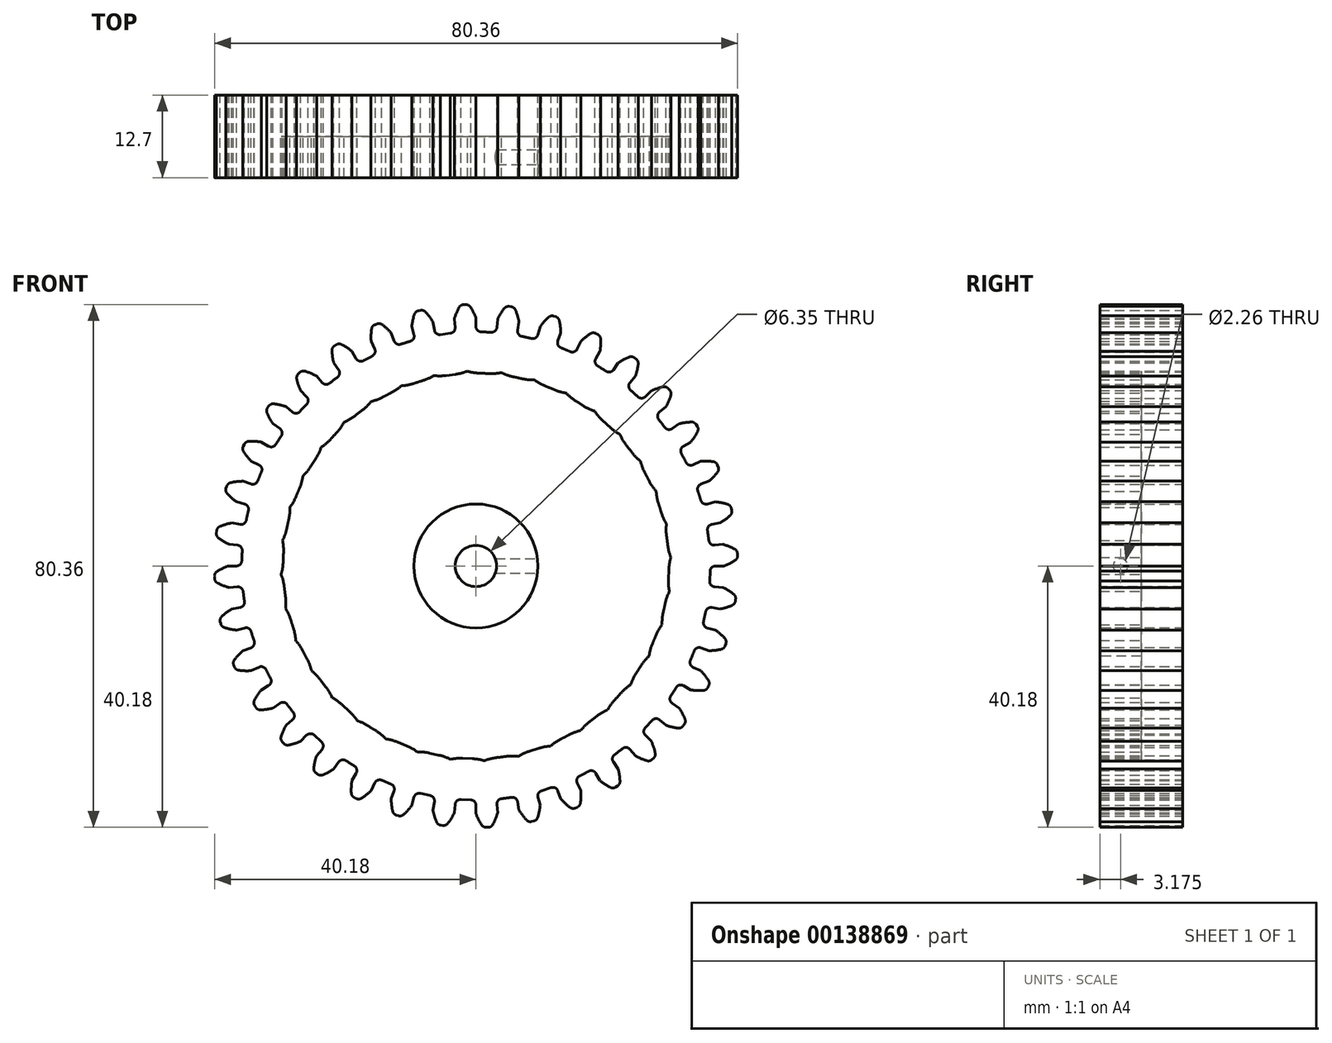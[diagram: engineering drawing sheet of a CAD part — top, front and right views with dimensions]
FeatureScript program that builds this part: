
annotation { "Feature Type Name" : "Feature", "Feature Type Description" : "" }
export const myFeature = defineFeature(function(context is Context, id is Id, definition is map)
    precondition{}
    {
        {
            var Q0;
            Q0=qCreatedBy(makeId("Front.planeOp"),FACE);
            var sketch = newSketch(context, id + "F0", { "sketchPlane" : qUnion([Q0])});
            skArc(sketch, "E0.trimOffspring", {"start": v(0, 38.1) * mm, "mid": v(-0.39, 38.97) * mm, "end": v(-0.86, 39.8) * mm});
            skLineSegment(sketch, "E1", {"start": v(0, 38.1) * mm, "end": v(0, 36.8) * mm});
            skLineSegment(sketch, "E2", {"start": v(-1.59, 40.18) * mm, "end": v(-1.75, 40.17) * mm});
            skLineSegment(sketch, "E3.MirrorCS", {"start": v(-1.92, 40.17) * mm, "end": v(-1.75, 40.17) * mm});
            skArc(sketch, "E4.MirrorCS", {"start": v(-3.32, 37.96) * mm, "mid": v(-3.01, 38.86) * mm, "end": v(-2.61, 39.72) * mm});
            skLineSegment(sketch, "E5.MirrorCS", {"start": v(-3.32, 37.96) * mm, "end": v(-3.2, 36.66) * mm});
            skPoint(sketch, "E6.visualSharp", {"position": v(-3.14, 35.85) * mm});
            skArc(sketch, "E6.filletArc", {"start": v(-3.94, 35.77) * mm, "mid": v(-3.4, 36.06) * mm, "end": v(-3.2, 36.66) * mm});
            skPoint(sketch, "E7.visualSharp", {"position": v(0, 35.98) * mm});
            skArc(sketch, "E7.filletArc", {"start": v(0, 36.8) * mm, "mid": v(0.24, 36.22) * mm, "end": v(0.8, 35.97) * mm});
            skArc(sketch, "E8.filletArc", {"start": v(-1.92, 40.17) * mm, "mid": v(-2.33, 40.04) * mm, "end": v(-2.61, 39.72) * mm});
            skArc(sketch, "E9.filletArc", {"start": v(-0.86, 39.8) * mm, "mid": v(-1.17, 40.09) * mm, "end": v(-1.59, 40.18) * mm});
            skArc(sketch, "E10.1.0", {"start": v(-10.1, 34.54) * mm, "mid": v(-9.6, 34.93) * mm, "end": v(-9.52, 35.55) * mm});
            skLineSegment(sketch, "E10.1.1", {"start": v(-9.86, 36.8) * mm, "end": v(-9.52, 35.55) * mm});
            skArc(sketch, "E10.1.2", {"start": v(-9.86, 36.8) * mm, "mid": v(-9.71, 37.74) * mm, "end": v(-9.47, 38.66) * mm});
            skArc(sketch, "E10.1.3", {"start": v(-8.86, 39.22) * mm, "mid": v(-9.24, 39.03) * mm, "end": v(-9.47, 38.66) * mm});
            skLineSegment(sketch, "E10.1.4", {"start": v(-8.86, 39.22) * mm, "end": v(-8.7, 39.26) * mm});
            skLineSegment(sketch, "E10.1.5", {"start": v(-8.54, 39.3) * mm, "end": v(-8.7, 39.26) * mm});
            skArc(sketch, "E10.1.6", {"start": v(-7.76, 39.05) * mm, "mid": v(-8.12, 39.28) * mm, "end": v(-8.54, 39.3) * mm});
            skArc(sketch, "E10.1.7", {"start": v(-6.62, 37.52) * mm, "mid": v(-7.15, 38.31) * mm, "end": v(-7.76, 39.05) * mm});
            skLineSegment(sketch, "E10.1.8", {"start": v(-6.62, 37.52) * mm, "end": v(-6.4, 36.24) * mm});
            skArc(sketch, "E10.1.9", {"start": v(-6.4, 36.24) * mm, "mid": v(-6.06, 35.71) * mm, "end": v(-5.45, 35.57) * mm});
            skArc(sketch, "E10.2.0", {"start": v(-15.93, 32.26) * mm, "mid": v(-15.52, 32.73) * mm, "end": v(-15.55, 33.35) * mm});
            skLineSegment(sketch, "E10.2.1", {"start": v(-16.1, 34.53) * mm, "end": v(-15.55, 33.35) * mm});
            skArc(sketch, "E10.2.2", {"start": v(-16.1, 34.53) * mm, "mid": v(-16.12, 35.48) * mm, "end": v(-16.04, 36.43) * mm});
            skArc(sketch, "E10.2.3", {"start": v(-15.54, 37.09) * mm, "mid": v(-15.88, 36.83) * mm, "end": v(-16.04, 36.43) * mm});
            skLineSegment(sketch, "E10.2.4", {"start": v(-15.54, 37.09) * mm, "end": v(-15.39, 37.15) * mm});
            skLineSegment(sketch, "E10.2.5", {"start": v(-15.24, 37.21) * mm, "end": v(-15.39, 37.15) * mm});
            skArc(sketch, "E10.2.6", {"start": v(-14.42, 37.1) * mm, "mid": v(-14.81, 37.27) * mm, "end": v(-15.24, 37.21) * mm});
            skArc(sketch, "E10.2.7", {"start": v(-13.03, 35.8) * mm, "mid": v(-13.7, 36.49) * mm, "end": v(-14.42, 37.1) * mm});
            skLineSegment(sketch, "E10.2.8", {"start": v(-13.03, 35.8) * mm, "end": v(-12.59, 34.58) * mm});
            skArc(sketch, "E10.2.9", {"start": v(-12.59, 34.58) * mm, "mid": v(-12.17, 34.12) * mm, "end": v(-11.55, 34.08) * mm});
            skArc(sketch, "E10.3.0", {"start": v(-21.3, 29) * mm, "mid": v(-20.97, 29.54) * mm, "end": v(-21.1, 30.14) * mm});
            skLineSegment(sketch, "E10.3.1", {"start": v(-21.85, 31.2) * mm, "end": v(-21.1, 30.14) * mm});
            skArc(sketch, "E10.3.2", {"start": v(-21.85, 31.2) * mm, "mid": v(-22.04, 32.14) * mm, "end": v(-22.13, 33.1) * mm});
            skArc(sketch, "E10.3.3", {"start": v(-21.74, 33.83) * mm, "mid": v(-22.03, 33.51) * mm, "end": v(-22.13, 33.1) * mm});
            skLineSegment(sketch, "E10.3.4", {"start": v(-21.74, 33.83) * mm, "end": v(-21.6, 33.91) * mm});
            skLineSegment(sketch, "E10.3.5", {"start": v(-21.47, 34) * mm, "end": v(-21.6, 33.91) * mm});
            skArc(sketch, "E10.3.6", {"start": v(-20.64, 34.04) * mm, "mid": v(-21.06, 34.13) * mm, "end": v(-21.47, 34) * mm});
            skArc(sketch, "E10.3.7", {"start": v(-19.05, 33) * mm, "mid": v(-19.82, 33.56) * mm, "end": v(-20.64, 34.04) * mm});
            skLineSegment(sketch, "E10.3.8", {"start": v(-19.05, 33) * mm, "end": v(-18.4, 31.87) * mm});
            skArc(sketch, "E10.3.9", {"start": v(-18.4, 31.87) * mm, "mid": v(-17.9, 31.49) * mm, "end": v(-17.29, 31.56) * mm});
            skArc(sketch, "E10.4.0", {"start": v(-26, 24.87) * mm, "mid": v(-25.78, 25.45) * mm, "end": v(-26.02, 26.02) * mm});
            skLineSegment(sketch, "E10.4.1", {"start": v(-26.94, 26.94) * mm, "end": v(-26.02, 26.02) * mm});
            skArc(sketch, "E10.4.2", {"start": v(-26.94, 26.94) * mm, "mid": v(-27.28, 27.83) * mm, "end": v(-27.54, 28.75) * mm});
            skArc(sketch, "E10.4.3", {"start": v(-27.29, 29.54) * mm, "mid": v(-27.52, 29.18) * mm, "end": v(-27.54, 28.75) * mm});
            skLineSegment(sketch, "E10.4.4", {"start": v(-27.29, 29.54) * mm, "end": v(-27.17, 29.65) * mm});
            skLineSegment(sketch, "E10.4.5", {"start": v(-27.05, 29.76) * mm, "end": v(-27.17, 29.65) * mm});
            skArc(sketch, "E10.4.6", {"start": v(-26.24, 29.94) * mm, "mid": v(-26.67, 29.96) * mm, "end": v(-27.05, 29.76) * mm});
            skArc(sketch, "E10.4.7", {"start": v(-24.5, 29.19) * mm, "mid": v(-25.35, 29.6) * mm, "end": v(-26.24, 29.94) * mm});
            skLineSegment(sketch, "E10.4.8", {"start": v(-24.5, 29.19) * mm, "end": v(-23.65, 28.2) * mm});
            skArc(sketch, "E10.4.9", {"start": v(-23.65, 28.2) * mm, "mid": v(-23.1, 27.9) * mm, "end": v(-22.5, 28.08) * mm});
            skArc(sketch, "E10.5.0", {"start": v(-29.93, 19.97) * mm, "mid": v(-29.8, 20.58) * mm, "end": v(-30.14, 21.1) * mm});
            skLineSegment(sketch, "E10.5.1", {"start": v(-31.2, 21.85) * mm, "end": v(-30.14, 21.1) * mm});
            skArc(sketch, "E10.5.2", {"start": v(-31.2, 21.85) * mm, "mid": v(-31.7, 22.67) * mm, "end": v(-32.1, 23.53) * mm});
            skArc(sketch, "E10.5.3", {"start": v(-32, 24.35) * mm, "mid": v(-32.17, 23.95) * mm, "end": v(-32.1, 23.53) * mm});
            skLineSegment(sketch, "E10.5.4", {"start": v(-32, 24.35) * mm, "end": v(-31.9, 24.48) * mm});
            skLineSegment(sketch, "E10.5.5", {"start": v(-31.8, 24.6) * mm, "end": v(-31.9, 24.48) * mm});
            skArc(sketch, "E10.5.6", {"start": v(-31.04, 24.93) * mm, "mid": v(-31.46, 24.87) * mm, "end": v(-31.8, 24.6) * mm});
            skArc(sketch, "E10.5.7", {"start": v(-29.19, 24.5) * mm, "mid": v(-30.1, 24.75) * mm, "end": v(-31.04, 24.93) * mm});
            skLineSegment(sketch, "E10.5.8", {"start": v(-29.19, 24.5) * mm, "end": v(-28.2, 23.65) * mm});
            skArc(sketch, "E10.5.9", {"start": v(-28.2, 23.65) * mm, "mid": v(-27.6, 23.46) * mm, "end": v(-27.04, 23.74) * mm});
            skArc(sketch, "E10.6.0", {"start": v(-32.94, 14.47) * mm, "mid": v(-32.93, 15.1) * mm, "end": v(-33.35, 15.55) * mm});
            skLineSegment(sketch, "E10.6.1", {"start": v(-34.53, 16.1) * mm, "end": v(-33.35, 15.55) * mm});
            skArc(sketch, "E10.6.2", {"start": v(-34.53, 16.1) * mm, "mid": v(-35.16, 16.82) * mm, "end": v(-35.7, 17.6) * mm});
            skArc(sketch, "E10.6.3", {"start": v(-35.74, 18.42) * mm, "mid": v(-35.84, 18) * mm, "end": v(-35.7, 17.6) * mm});
            skLineSegment(sketch, "E10.6.4", {"start": v(-35.74, 18.42) * mm, "end": v(-35.67, 18.57) * mm});
            skLineSegment(sketch, "E10.6.5", {"start": v(-35.6, 18.71) * mm, "end": v(-35.67, 18.57) * mm});
            skArc(sketch, "E10.6.6", {"start": v(-34.9, 19.16) * mm, "mid": v(-35.3, 19.03) * mm, "end": v(-35.6, 18.71) * mm});
            skArc(sketch, "E10.6.7", {"start": v(-33, 19.05) * mm, "mid": v(-33.94, 19.15) * mm, "end": v(-34.9, 19.16) * mm});
            skLineSegment(sketch, "E10.6.8", {"start": v(-33, 19.05) * mm, "end": v(-31.87, 18.4) * mm});
            skArc(sketch, "E10.6.9", {"start": v(-31.87, 18.4) * mm, "mid": v(-31.25, 18.31) * mm, "end": v(-30.75, 18.69) * mm});
            skArc(sketch, "E10.7.0", {"start": v(-34.96, 8.53) * mm, "mid": v(-35.05, 9.15) * mm, "end": v(-35.55, 9.52) * mm});
            skLineSegment(sketch, "E10.7.1", {"start": v(-36.8, 9.86) * mm, "end": v(-35.55, 9.52) * mm});
            skArc(sketch, "E10.7.2", {"start": v(-36.8, 9.86) * mm, "mid": v(-37.54, 10.46) * mm, "end": v(-38.22, 11.13) * mm});
            skArc(sketch, "E10.7.3", {"start": v(-38.4, 11.93) * mm, "mid": v(-38.42, 11.5) * mm, "end": v(-38.22, 11.13) * mm});
            skLineSegment(sketch, "E10.7.4", {"start": v(-38.4, 11.93) * mm, "end": v(-38.35, 12.1) * mm});
            skLineSegment(sketch, "E10.7.5", {"start": v(-38.3, 12.25) * mm, "end": v(-38.35, 12.1) * mm});
            skArc(sketch, "E10.7.6", {"start": v(-37.7, 12.8) * mm, "mid": v(-38.07, 12.6) * mm, "end": v(-38.3, 12.25) * mm});
            skArc(sketch, "E10.7.7", {"start": v(-35.8, 13.03) * mm, "mid": v(-36.75, 12.97) * mm, "end": v(-37.7, 12.8) * mm});
            skLineSegment(sketch, "E10.7.8", {"start": v(-35.8, 13.03) * mm, "end": v(-34.58, 12.59) * mm});
            skArc(sketch, "E10.7.9", {"start": v(-34.58, 12.59) * mm, "mid": v(-33.96, 12.6) * mm, "end": v(-33.53, 13.06) * mm});
            skArc(sketch, "E10.8.0", {"start": v(-35.9, 2.33) * mm, "mid": v(-36.1, 2.92) * mm, "end": v(-36.66, 3.2) * mm});
            skLineSegment(sketch, "E10.8.1", {"start": v(-37.96, 3.32) * mm, "end": v(-36.66, 3.2) * mm});
            skArc(sketch, "E10.8.2", {"start": v(-37.96, 3.32) * mm, "mid": v(-38.79, 3.78) * mm, "end": v(-39.57, 4.32) * mm});
            skArc(sketch, "E10.8.3", {"start": v(-39.89, 5.09) * mm, "mid": v(-39.83, 4.66) * mm, "end": v(-39.57, 4.32) * mm});
            skLineSegment(sketch, "E10.8.4", {"start": v(-39.89, 5.09) * mm, "end": v(-39.87, 5.25) * mm});
            skLineSegment(sketch, "E10.8.5", {"start": v(-39.85, 5.41) * mm, "end": v(-39.87, 5.25) * mm});
            skArc(sketch, "E10.8.6", {"start": v(-39.34, 6.07) * mm, "mid": v(-39.68, 5.8) * mm, "end": v(-39.85, 5.41) * mm});
            skArc(sketch, "E10.8.7", {"start": v(-37.52, 6.62) * mm, "mid": v(-38.45, 6.39) * mm, "end": v(-39.34, 6.07) * mm});
            skLineSegment(sketch, "E10.8.8", {"start": v(-37.52, 6.62) * mm, "end": v(-36.24, 6.4) * mm});
            skArc(sketch, "E10.8.9", {"start": v(-36.24, 6.4) * mm, "mid": v(-35.63, 6.52) * mm, "end": v(-35.29, 7.04) * mm});
            skArc(sketch, "E10.9.0", {"start": v(-35.77, -3.94) * mm, "mid": v(-36.06, -3.4) * mm, "end": v(-36.66, -3.2) * mm});
            skLineSegment(sketch, "E10.9.1", {"start": v(-37.96, -3.32) * mm, "end": v(-36.66, -3.2) * mm});
            skArc(sketch, "E10.9.2", {"start": v(-37.96, -3.32) * mm, "mid": v(-38.86, -3.01) * mm, "end": v(-39.72, -2.61) * mm});
            skArc(sketch, "E10.9.3", {"start": v(-40.17, -1.92) * mm, "mid": v(-40.04, -2.33) * mm, "end": v(-39.72, -2.61) * mm});
            skLineSegment(sketch, "E10.9.4", {"start": v(-40.17, -1.92) * mm, "end": v(-40.17, -1.75) * mm});
            skLineSegment(sketch, "E10.9.5", {"start": v(-40.18, -1.59) * mm, "end": v(-40.17, -1.75) * mm});
            skArc(sketch, "E10.9.6", {"start": v(-39.8, -0.86) * mm, "mid": v(-40.09, -1.17) * mm, "end": v(-40.18, -1.59) * mm});
            skArc(sketch, "E10.9.7", {"start": v(-38.1, 0) * mm, "mid": v(-38.97, -0.39) * mm, "end": v(-39.8, -0.86) * mm});
            skLineSegment(sketch, "E10.9.8", {"start": v(-38.1, 0) * mm, "end": v(-36.8, 0) * mm});
            skArc(sketch, "E10.9.9", {"start": v(-36.8, 0) * mm, "mid": v(-36.22, 0.24) * mm, "end": v(-35.97, 0.8) * mm});
            skArc(sketch, "E10.10.0", {"start": v(-34.54, -10.1) * mm, "mid": v(-34.93, -9.6) * mm, "end": v(-35.55, -9.52) * mm});
            skLineSegment(sketch, "E10.10.1", {"start": v(-36.8, -9.86) * mm, "end": v(-35.55, -9.52) * mm});
            skArc(sketch, "E10.10.2", {"start": v(-36.8, -9.86) * mm, "mid": v(-37.74, -9.71) * mm, "end": v(-38.66, -9.47) * mm});
            skArc(sketch, "E10.10.3", {"start": v(-39.22, -8.86) * mm, "mid": v(-39.03, -9.24) * mm, "end": v(-38.66, -9.47) * mm});
            skLineSegment(sketch, "E10.10.4", {"start": v(-39.22, -8.86) * mm, "end": v(-39.26, -8.7) * mm});
            skLineSegment(sketch, "E10.10.5", {"start": v(-39.3, -8.54) * mm, "end": v(-39.26, -8.7) * mm});
            skArc(sketch, "E10.10.6", {"start": v(-39.05, -7.76) * mm, "mid": v(-39.28, -8.12) * mm, "end": v(-39.3, -8.54) * mm});
            skArc(sketch, "E10.10.7", {"start": v(-37.52, -6.62) * mm, "mid": v(-38.31, -7.15) * mm, "end": v(-39.05, -7.76) * mm});
            skLineSegment(sketch, "E10.10.8", {"start": v(-37.52, -6.62) * mm, "end": v(-36.24, -6.4) * mm});
            skArc(sketch, "E10.10.9", {"start": v(-36.24, -6.4) * mm, "mid": v(-35.71, -6.06) * mm, "end": v(-35.57, -5.45) * mm});
            skArc(sketch, "E10.11.0", {"start": v(-32.26, -15.93) * mm, "mid": v(-32.73, -15.52) * mm, "end": v(-33.35, -15.55) * mm});
            skLineSegment(sketch, "E10.11.1", {"start": v(-34.53, -16.1) * mm, "end": v(-33.35, -15.55) * mm});
            skArc(sketch, "E10.11.2", {"start": v(-34.53, -16.1) * mm, "mid": v(-35.48, -16.12) * mm, "end": v(-36.43, -16.04) * mm});
            skArc(sketch, "E10.11.3", {"start": v(-37.09, -15.54) * mm, "mid": v(-36.83, -15.88) * mm, "end": v(-36.43, -16.04) * mm});
            skLineSegment(sketch, "E10.11.4", {"start": v(-37.09, -15.54) * mm, "end": v(-37.15, -15.39) * mm});
            skLineSegment(sketch, "E10.11.5", {"start": v(-37.21, -15.24) * mm, "end": v(-37.15, -15.39) * mm});
            skArc(sketch, "E10.11.6", {"start": v(-37.1, -14.42) * mm, "mid": v(-37.27, -14.81) * mm, "end": v(-37.21, -15.24) * mm});
            skArc(sketch, "E10.11.7", {"start": v(-35.8, -13.03) * mm, "mid": v(-36.49, -13.7) * mm, "end": v(-37.1, -14.42) * mm});
            skLineSegment(sketch, "E10.11.8", {"start": v(-35.8, -13.03) * mm, "end": v(-34.58, -12.59) * mm});
            skArc(sketch, "E10.11.9", {"start": v(-34.58, -12.59) * mm, "mid": v(-34.12, -12.17) * mm, "end": v(-34.08, -11.55) * mm});
            skArc(sketch, "E10.12.0", {"start": v(-29, -21.3) * mm, "mid": v(-29.54, -20.97) * mm, "end": v(-30.14, -21.1) * mm});
            skLineSegment(sketch, "E10.12.1", {"start": v(-31.2, -21.85) * mm, "end": v(-30.14, -21.1) * mm});
            skArc(sketch, "E10.12.2", {"start": v(-31.2, -21.85) * mm, "mid": v(-32.14, -22.04) * mm, "end": v(-33.1, -22.13) * mm});
            skArc(sketch, "E10.12.3", {"start": v(-33.83, -21.74) * mm, "mid": v(-33.51, -22.03) * mm, "end": v(-33.1, -22.13) * mm});
            skLineSegment(sketch, "E10.12.4", {"start": v(-33.83, -21.74) * mm, "end": v(-33.91, -21.6) * mm});
            skLineSegment(sketch, "E10.12.5", {"start": v(-34, -21.47) * mm, "end": v(-33.91, -21.6) * mm});
            skArc(sketch, "E10.12.6", {"start": v(-34.04, -20.64) * mm, "mid": v(-34.13, -21.06) * mm, "end": v(-34, -21.47) * mm});
            skArc(sketch, "E10.12.7", {"start": v(-33, -19.05) * mm, "mid": v(-33.56, -19.82) * mm, "end": v(-34.04, -20.64) * mm});
            skLineSegment(sketch, "E10.12.8", {"start": v(-33, -19.05) * mm, "end": v(-31.87, -18.4) * mm});
            skArc(sketch, "E10.12.9", {"start": v(-31.87, -18.4) * mm, "mid": v(-31.49, -17.9) * mm, "end": v(-31.56, -17.29) * mm});
            skArc(sketch, "E10.13.0", {"start": v(-24.87, -26) * mm, "mid": v(-25.45, -25.78) * mm, "end": v(-26.02, -26.02) * mm});
            skLineSegment(sketch, "E10.13.1", {"start": v(-26.94, -26.94) * mm, "end": v(-26.02, -26.02) * mm});
            skArc(sketch, "E10.13.2", {"start": v(-26.94, -26.94) * mm, "mid": v(-27.83, -27.28) * mm, "end": v(-28.75, -27.54) * mm});
            skArc(sketch, "E10.13.3", {"start": v(-29.54, -27.29) * mm, "mid": v(-29.18, -27.52) * mm, "end": v(-28.75, -27.54) * mm});
            skLineSegment(sketch, "E10.13.4", {"start": v(-29.54, -27.29) * mm, "end": v(-29.65, -27.17) * mm});
            skLineSegment(sketch, "E10.13.5", {"start": v(-29.76, -27.05) * mm, "end": v(-29.65, -27.17) * mm});
            skArc(sketch, "E10.13.6", {"start": v(-29.94, -26.24) * mm, "mid": v(-29.96, -26.67) * mm, "end": v(-29.76, -27.05) * mm});
            skArc(sketch, "E10.13.7", {"start": v(-29.19, -24.5) * mm, "mid": v(-29.6, -25.35) * mm, "end": v(-29.94, -26.24) * mm});
            skLineSegment(sketch, "E10.13.8", {"start": v(-29.19, -24.5) * mm, "end": v(-28.2, -23.65) * mm});
            skArc(sketch, "E10.13.9", {"start": v(-28.2, -23.65) * mm, "mid": v(-27.9, -23.1) * mm, "end": v(-28.08, -22.5) * mm});
            skArc(sketch, "E10.14.0", {"start": v(-19.97, -29.93) * mm, "mid": v(-20.58, -29.8) * mm, "end": v(-21.1, -30.14) * mm});
            skLineSegment(sketch, "E10.14.1", {"start": v(-21.85, -31.2) * mm, "end": v(-21.1, -30.14) * mm});
            skArc(sketch, "E10.14.2", {"start": v(-21.85, -31.2) * mm, "mid": v(-22.67, -31.7) * mm, "end": v(-23.53, -32.1) * mm});
            skArc(sketch, "E10.14.3", {"start": v(-24.35, -32) * mm, "mid": v(-23.95, -32.17) * mm, "end": v(-23.53, -32.1) * mm});
            skLineSegment(sketch, "E10.14.4", {"start": v(-24.35, -32) * mm, "end": v(-24.48, -31.9) * mm});
            skLineSegment(sketch, "E10.14.5", {"start": v(-24.6, -31.8) * mm, "end": v(-24.48, -31.9) * mm});
            skArc(sketch, "E10.14.6", {"start": v(-24.93, -31.04) * mm, "mid": v(-24.87, -31.46) * mm, "end": v(-24.6, -31.8) * mm});
            skArc(sketch, "E10.14.7", {"start": v(-24.5, -29.19) * mm, "mid": v(-24.75, -30.1) * mm, "end": v(-24.93, -31.04) * mm});
            skLineSegment(sketch, "E10.14.8", {"start": v(-24.5, -29.19) * mm, "end": v(-23.65, -28.2) * mm});
            skArc(sketch, "E10.14.9", {"start": v(-23.65, -28.2) * mm, "mid": v(-23.46, -27.6) * mm, "end": v(-23.74, -27.04) * mm});
            skArc(sketch, "E10.15.0", {"start": v(-14.47, -32.94) * mm, "mid": v(-15.1, -32.93) * mm, "end": v(-15.55, -33.35) * mm});
            skLineSegment(sketch, "E10.15.1", {"start": v(-16.1, -34.53) * mm, "end": v(-15.55, -33.35) * mm});
            skArc(sketch, "E10.15.2", {"start": v(-16.1, -34.53) * mm, "mid": v(-16.82, -35.16) * mm, "end": v(-17.6, -35.7) * mm});
            skArc(sketch, "E10.15.3", {"start": v(-18.42, -35.74) * mm, "mid": v(-18, -35.84) * mm, "end": v(-17.6, -35.7) * mm});
            skLineSegment(sketch, "E10.15.4", {"start": v(-18.42, -35.74) * mm, "end": v(-18.57, -35.67) * mm});
            skLineSegment(sketch, "E10.15.5", {"start": v(-18.71, -35.6) * mm, "end": v(-18.57, -35.67) * mm});
            skArc(sketch, "E10.15.6", {"start": v(-19.16, -34.9) * mm, "mid": v(-19.03, -35.3) * mm, "end": v(-18.71, -35.6) * mm});
            skArc(sketch, "E10.15.7", {"start": v(-19.05, -33) * mm, "mid": v(-19.15, -33.94) * mm, "end": v(-19.16, -34.9) * mm});
            skLineSegment(sketch, "E10.15.8", {"start": v(-19.05, -33) * mm, "end": v(-18.4, -31.87) * mm});
            skArc(sketch, "E10.15.9", {"start": v(-18.4, -31.87) * mm, "mid": v(-18.31, -31.25) * mm, "end": v(-18.69, -30.75) * mm});
            skArc(sketch, "E10.16.0", {"start": v(-8.53, -34.96) * mm, "mid": v(-9.15, -35.05) * mm, "end": v(-9.52, -35.55) * mm});
            skLineSegment(sketch, "E10.16.1", {"start": v(-9.86, -36.8) * mm, "end": v(-9.52, -35.55) * mm});
            skArc(sketch, "E10.16.2", {"start": v(-9.86, -36.8) * mm, "mid": v(-10.46, -37.54) * mm, "end": v(-11.13, -38.22) * mm});
            skArc(sketch, "E10.16.3", {"start": v(-11.93, -38.4) * mm, "mid": v(-11.5, -38.42) * mm, "end": v(-11.13, -38.22) * mm});
            skLineSegment(sketch, "E10.16.4", {"start": v(-11.93, -38.4) * mm, "end": v(-12.1, -38.35) * mm});
            skLineSegment(sketch, "E10.16.5", {"start": v(-12.25, -38.3) * mm, "end": v(-12.1, -38.35) * mm});
            skArc(sketch, "E10.16.6", {"start": v(-12.8, -37.7) * mm, "mid": v(-12.6, -38.07) * mm, "end": v(-12.25, -38.3) * mm});
            skArc(sketch, "E10.16.7", {"start": v(-13.03, -35.8) * mm, "mid": v(-12.97, -36.75) * mm, "end": v(-12.8, -37.7) * mm});
            skLineSegment(sketch, "E10.16.8", {"start": v(-13.03, -35.8) * mm, "end": v(-12.59, -34.58) * mm});
            skArc(sketch, "E10.16.9", {"start": v(-12.59, -34.58) * mm, "mid": v(-12.6, -33.96) * mm, "end": v(-13.06, -33.53) * mm});
            skArc(sketch, "E10.17.0", {"start": v(-2.33, -35.9) * mm, "mid": v(-2.92, -36.1) * mm, "end": v(-3.2, -36.66) * mm});
            skLineSegment(sketch, "E10.17.1", {"start": v(-3.32, -37.96) * mm, "end": v(-3.2, -36.66) * mm});
            skArc(sketch, "E10.17.2", {"start": v(-3.32, -37.96) * mm, "mid": v(-3.78, -38.79) * mm, "end": v(-4.32, -39.57) * mm});
            skArc(sketch, "E10.17.3", {"start": v(-5.09, -39.89) * mm, "mid": v(-4.66, -39.83) * mm, "end": v(-4.32, -39.57) * mm});
            skLineSegment(sketch, "E10.17.4", {"start": v(-5.09, -39.89) * mm, "end": v(-5.25, -39.87) * mm});
            skLineSegment(sketch, "E10.17.5", {"start": v(-5.41, -39.85) * mm, "end": v(-5.25, -39.87) * mm});
            skArc(sketch, "E10.17.6", {"start": v(-6.07, -39.34) * mm, "mid": v(-5.8, -39.68) * mm, "end": v(-5.41, -39.85) * mm});
            skArc(sketch, "E10.17.7", {"start": v(-6.62, -37.52) * mm, "mid": v(-6.39, -38.45) * mm, "end": v(-6.07, -39.34) * mm});
            skLineSegment(sketch, "E10.17.8", {"start": v(-6.62, -37.52) * mm, "end": v(-6.4, -36.24) * mm});
            skArc(sketch, "E10.17.9", {"start": v(-6.4, -36.24) * mm, "mid": v(-6.52, -35.63) * mm, "end": v(-7.04, -35.29) * mm});
            skArc(sketch, "E10.18.0", {"start": v(3.94, -35.77) * mm, "mid": v(3.4, -36.06) * mm, "end": v(3.2, -36.66) * mm});
            skLineSegment(sketch, "E10.18.1", {"start": v(3.32, -37.96) * mm, "end": v(3.2, -36.66) * mm});
            skArc(sketch, "E10.18.2", {"start": v(3.32, -37.96) * mm, "mid": v(3.01, -38.86) * mm, "end": v(2.61, -39.72) * mm});
            skArc(sketch, "E10.18.3", {"start": v(1.92, -40.17) * mm, "mid": v(2.33, -40.04) * mm, "end": v(2.61, -39.72) * mm});
            skLineSegment(sketch, "E10.18.4", {"start": v(1.92, -40.17) * mm, "end": v(1.75, -40.17) * mm});
            skLineSegment(sketch, "E10.18.5", {"start": v(1.59, -40.18) * mm, "end": v(1.75, -40.17) * mm});
            skArc(sketch, "E10.18.6", {"start": v(0.86, -39.8) * mm, "mid": v(1.17, -40.09) * mm, "end": v(1.59, -40.18) * mm});
            skArc(sketch, "E10.18.7", {"start": v(0, -38.1) * mm, "mid": v(0.39, -38.97) * mm, "end": v(0.86, -39.8) * mm});
            skLineSegment(sketch, "E10.18.8", {"start": v(0, -38.1) * mm, "end": v(0, -36.8) * mm});
            skArc(sketch, "E10.18.9", {"start": v(0, -36.8) * mm, "mid": v(-0.24, -36.22) * mm, "end": v(-0.8, -35.97) * mm});
            skArc(sketch, "E10.19.0", {"start": v(10.1, -34.54) * mm, "mid": v(9.6, -34.93) * mm, "end": v(9.52, -35.55) * mm});
            skLineSegment(sketch, "E10.19.1", {"start": v(9.86, -36.8) * mm, "end": v(9.52, -35.55) * mm});
            skArc(sketch, "E10.19.2", {"start": v(9.86, -36.8) * mm, "mid": v(9.71, -37.74) * mm, "end": v(9.47, -38.66) * mm});
            skArc(sketch, "E10.19.3", {"start": v(8.86, -39.22) * mm, "mid": v(9.24, -39.03) * mm, "end": v(9.47, -38.66) * mm});
            skLineSegment(sketch, "E10.19.4", {"start": v(8.86, -39.22) * mm, "end": v(8.7, -39.26) * mm});
            skLineSegment(sketch, "E10.19.5", {"start": v(8.54, -39.3) * mm, "end": v(8.7, -39.26) * mm});
            skArc(sketch, "E10.19.6", {"start": v(7.76, -39.05) * mm, "mid": v(8.12, -39.28) * mm, "end": v(8.54, -39.3) * mm});
            skArc(sketch, "E10.19.7", {"start": v(6.62, -37.52) * mm, "mid": v(7.15, -38.31) * mm, "end": v(7.76, -39.05) * mm});
            skLineSegment(sketch, "E10.19.8", {"start": v(6.62, -37.52) * mm, "end": v(6.4, -36.24) * mm});
            skArc(sketch, "E10.19.9", {"start": v(6.4, -36.24) * mm, "mid": v(6.06, -35.71) * mm, "end": v(5.45, -35.57) * mm});
            skArc(sketch, "E10.20.0", {"start": v(15.93, -32.26) * mm, "mid": v(15.52, -32.73) * mm, "end": v(15.55, -33.35) * mm});
            skLineSegment(sketch, "E10.20.1", {"start": v(16.1, -34.53) * mm, "end": v(15.55, -33.35) * mm});
            skArc(sketch, "E10.20.2", {"start": v(16.1, -34.53) * mm, "mid": v(16.12, -35.48) * mm, "end": v(16.04, -36.43) * mm});
            skArc(sketch, "E10.20.3", {"start": v(15.54, -37.09) * mm, "mid": v(15.88, -36.83) * mm, "end": v(16.04, -36.43) * mm});
            skLineSegment(sketch, "E10.20.4", {"start": v(15.54, -37.09) * mm, "end": v(15.39, -37.15) * mm});
            skLineSegment(sketch, "E10.20.5", {"start": v(15.24, -37.21) * mm, "end": v(15.39, -37.15) * mm});
            skArc(sketch, "E10.20.6", {"start": v(14.42, -37.1) * mm, "mid": v(14.81, -37.27) * mm, "end": v(15.24, -37.21) * mm});
            skArc(sketch, "E10.20.7", {"start": v(13.03, -35.8) * mm, "mid": v(13.7, -36.49) * mm, "end": v(14.42, -37.1) * mm});
            skLineSegment(sketch, "E10.20.8", {"start": v(13.03, -35.8) * mm, "end": v(12.59, -34.58) * mm});
            skArc(sketch, "E10.20.9", {"start": v(12.59, -34.58) * mm, "mid": v(12.17, -34.12) * mm, "end": v(11.55, -34.08) * mm});
            skArc(sketch, "E10.21.0", {"start": v(21.3, -29) * mm, "mid": v(20.97, -29.54) * mm, "end": v(21.1, -30.14) * mm});
            skLineSegment(sketch, "E10.21.1", {"start": v(21.85, -31.2) * mm, "end": v(21.1, -30.14) * mm});
            skArc(sketch, "E10.21.2", {"start": v(21.85, -31.2) * mm, "mid": v(22.04, -32.14) * mm, "end": v(22.13, -33.1) * mm});
            skArc(sketch, "E10.21.3", {"start": v(21.74, -33.83) * mm, "mid": v(22.03, -33.51) * mm, "end": v(22.13, -33.1) * mm});
            skLineSegment(sketch, "E10.21.4", {"start": v(21.74, -33.83) * mm, "end": v(21.6, -33.91) * mm});
            skLineSegment(sketch, "E10.21.5", {"start": v(21.47, -34) * mm, "end": v(21.6, -33.91) * mm});
            skArc(sketch, "E10.21.6", {"start": v(20.64, -34.04) * mm, "mid": v(21.06, -34.13) * mm, "end": v(21.47, -34) * mm});
            skArc(sketch, "E10.21.7", {"start": v(19.05, -33) * mm, "mid": v(19.82, -33.56) * mm, "end": v(20.64, -34.04) * mm});
            skLineSegment(sketch, "E10.21.8", {"start": v(19.05, -33) * mm, "end": v(18.4, -31.87) * mm});
            skArc(sketch, "E10.21.9", {"start": v(18.4, -31.87) * mm, "mid": v(17.9, -31.49) * mm, "end": v(17.29, -31.56) * mm});
            skArc(sketch, "E10.22.0", {"start": v(26, -24.87) * mm, "mid": v(25.78, -25.45) * mm, "end": v(26.02, -26.02) * mm});
            skLineSegment(sketch, "E10.22.1", {"start": v(26.94, -26.94) * mm, "end": v(26.02, -26.02) * mm});
            skArc(sketch, "E10.22.2", {"start": v(26.94, -26.94) * mm, "mid": v(27.28, -27.83) * mm, "end": v(27.54, -28.75) * mm});
            skArc(sketch, "E10.22.3", {"start": v(27.29, -29.54) * mm, "mid": v(27.52, -29.18) * mm, "end": v(27.54, -28.75) * mm});
            skLineSegment(sketch, "E10.22.4", {"start": v(27.29, -29.54) * mm, "end": v(27.17, -29.65) * mm});
            skLineSegment(sketch, "E10.22.5", {"start": v(27.05, -29.76) * mm, "end": v(27.17, -29.65) * mm});
            skArc(sketch, "E10.22.6", {"start": v(26.24, -29.94) * mm, "mid": v(26.67, -29.96) * mm, "end": v(27.05, -29.76) * mm});
            skArc(sketch, "E10.22.7", {"start": v(24.5, -29.19) * mm, "mid": v(25.35, -29.6) * mm, "end": v(26.24, -29.94) * mm});
            skLineSegment(sketch, "E10.22.8", {"start": v(24.5, -29.19) * mm, "end": v(23.65, -28.2) * mm});
            skArc(sketch, "E10.22.9", {"start": v(23.65, -28.2) * mm, "mid": v(23.1, -27.9) * mm, "end": v(22.5, -28.08) * mm});
            skArc(sketch, "E10.23.0", {"start": v(29.93, -19.97) * mm, "mid": v(29.8, -20.58) * mm, "end": v(30.14, -21.1) * mm});
            skLineSegment(sketch, "E10.23.1", {"start": v(31.2, -21.85) * mm, "end": v(30.14, -21.1) * mm});
            skArc(sketch, "E10.23.2", {"start": v(31.2, -21.85) * mm, "mid": v(31.7, -22.67) * mm, "end": v(32.1, -23.53) * mm});
            skArc(sketch, "E10.23.3", {"start": v(32, -24.35) * mm, "mid": v(32.17, -23.95) * mm, "end": v(32.1, -23.53) * mm});
            skLineSegment(sketch, "E10.23.4", {"start": v(32, -24.35) * mm, "end": v(31.9, -24.48) * mm});
            skLineSegment(sketch, "E10.23.5", {"start": v(31.8, -24.6) * mm, "end": v(31.9, -24.48) * mm});
            skArc(sketch, "E10.23.6", {"start": v(31.04, -24.93) * mm, "mid": v(31.46, -24.87) * mm, "end": v(31.8, -24.6) * mm});
            skArc(sketch, "E10.23.7", {"start": v(29.19, -24.5) * mm, "mid": v(30.1, -24.75) * mm, "end": v(31.04, -24.93) * mm});
            skLineSegment(sketch, "E10.23.8", {"start": v(29.19, -24.5) * mm, "end": v(28.2, -23.65) * mm});
            skArc(sketch, "E10.23.9", {"start": v(28.2, -23.65) * mm, "mid": v(27.6, -23.46) * mm, "end": v(27.04, -23.74) * mm});
            skArc(sketch, "E10.24.0", {"start": v(32.94, -14.47) * mm, "mid": v(32.93, -15.1) * mm, "end": v(33.35, -15.55) * mm});
            skLineSegment(sketch, "E10.24.1", {"start": v(34.53, -16.1) * mm, "end": v(33.35, -15.55) * mm});
            skArc(sketch, "E10.24.2", {"start": v(34.53, -16.1) * mm, "mid": v(35.16, -16.82) * mm, "end": v(35.7, -17.6) * mm});
            skArc(sketch, "E10.24.3", {"start": v(35.74, -18.42) * mm, "mid": v(35.84, -18) * mm, "end": v(35.7, -17.6) * mm});
            skLineSegment(sketch, "E10.24.4", {"start": v(35.74, -18.42) * mm, "end": v(35.67, -18.57) * mm});
            skLineSegment(sketch, "E10.24.5", {"start": v(35.6, -18.71) * mm, "end": v(35.67, -18.57) * mm});
            skArc(sketch, "E10.24.6", {"start": v(34.9, -19.16) * mm, "mid": v(35.3, -19.03) * mm, "end": v(35.6, -18.71) * mm});
            skArc(sketch, "E10.24.7", {"start": v(33, -19.05) * mm, "mid": v(33.94, -19.15) * mm, "end": v(34.9, -19.16) * mm});
            skLineSegment(sketch, "E10.24.8", {"start": v(33, -19.05) * mm, "end": v(31.87, -18.4) * mm});
            skArc(sketch, "E10.24.9", {"start": v(31.87, -18.4) * mm, "mid": v(31.25, -18.31) * mm, "end": v(30.75, -18.69) * mm});
            skArc(sketch, "E10.25.0", {"start": v(34.96, -8.53) * mm, "mid": v(35.05, -9.15) * mm, "end": v(35.55, -9.52) * mm});
            skLineSegment(sketch, "E10.25.1", {"start": v(36.8, -9.86) * mm, "end": v(35.55, -9.52) * mm});
            skArc(sketch, "E10.25.2", {"start": v(36.8, -9.86) * mm, "mid": v(37.54, -10.46) * mm, "end": v(38.22, -11.13) * mm});
            skArc(sketch, "E10.25.3", {"start": v(38.4, -11.93) * mm, "mid": v(38.42, -11.5) * mm, "end": v(38.22, -11.13) * mm});
            skLineSegment(sketch, "E10.25.4", {"start": v(38.4, -11.93) * mm, "end": v(38.35, -12.1) * mm});
            skLineSegment(sketch, "E10.25.5", {"start": v(38.3, -12.25) * mm, "end": v(38.35, -12.1) * mm});
            skArc(sketch, "E10.25.6", {"start": v(37.7, -12.8) * mm, "mid": v(38.07, -12.6) * mm, "end": v(38.3, -12.25) * mm});
            skArc(sketch, "E10.25.7", {"start": v(35.8, -13.03) * mm, "mid": v(36.75, -12.97) * mm, "end": v(37.7, -12.8) * mm});
            skLineSegment(sketch, "E10.25.8", {"start": v(35.8, -13.03) * mm, "end": v(34.58, -12.59) * mm});
            skArc(sketch, "E10.25.9", {"start": v(34.58, -12.59) * mm, "mid": v(33.96, -12.6) * mm, "end": v(33.53, -13.06) * mm});
            skArc(sketch, "E10.26.0", {"start": v(35.9, -2.33) * mm, "mid": v(36.1, -2.92) * mm, "end": v(36.66, -3.2) * mm});
            skLineSegment(sketch, "E10.26.1", {"start": v(37.96, -3.32) * mm, "end": v(36.66, -3.2) * mm});
            skArc(sketch, "E10.26.2", {"start": v(37.96, -3.32) * mm, "mid": v(38.79, -3.78) * mm, "end": v(39.57, -4.32) * mm});
            skArc(sketch, "E10.26.3", {"start": v(39.89, -5.09) * mm, "mid": v(39.83, -4.66) * mm, "end": v(39.57, -4.32) * mm});
            skLineSegment(sketch, "E10.26.4", {"start": v(39.89, -5.09) * mm, "end": v(39.87, -5.25) * mm});
            skLineSegment(sketch, "E10.26.5", {"start": v(39.85, -5.41) * mm, "end": v(39.87, -5.25) * mm});
            skArc(sketch, "E10.26.6", {"start": v(39.34, -6.07) * mm, "mid": v(39.68, -5.8) * mm, "end": v(39.85, -5.41) * mm});
            skArc(sketch, "E10.26.7", {"start": v(37.52, -6.62) * mm, "mid": v(38.45, -6.39) * mm, "end": v(39.34, -6.07) * mm});
            skLineSegment(sketch, "E10.26.8", {"start": v(37.52, -6.62) * mm, "end": v(36.24, -6.4) * mm});
            skArc(sketch, "E10.26.9", {"start": v(36.24, -6.4) * mm, "mid": v(35.63, -6.52) * mm, "end": v(35.29, -7.04) * mm});
            skArc(sketch, "E10.27.0", {"start": v(35.77, 3.94) * mm, "mid": v(36.06, 3.4) * mm, "end": v(36.66, 3.2) * mm});
            skLineSegment(sketch, "E10.27.1", {"start": v(37.96, 3.32) * mm, "end": v(36.66, 3.2) * mm});
            skArc(sketch, "E10.27.2", {"start": v(37.96, 3.32) * mm, "mid": v(38.86, 3.01) * mm, "end": v(39.72, 2.61) * mm});
            skArc(sketch, "E10.27.3", {"start": v(40.17, 1.92) * mm, "mid": v(40.04, 2.33) * mm, "end": v(39.72, 2.61) * mm});
            skLineSegment(sketch, "E10.27.4", {"start": v(40.17, 1.92) * mm, "end": v(40.17, 1.75) * mm});
            skLineSegment(sketch, "E10.27.5", {"start": v(40.18, 1.59) * mm, "end": v(40.17, 1.75) * mm});
            skArc(sketch, "E10.27.6", {"start": v(39.8, 0.86) * mm, "mid": v(40.09, 1.17) * mm, "end": v(40.18, 1.59) * mm});
            skArc(sketch, "E10.27.7", {"start": v(38.1, 0) * mm, "mid": v(38.97, 0.39) * mm, "end": v(39.8, 0.86) * mm});
            skLineSegment(sketch, "E10.27.8", {"start": v(38.1, 0) * mm, "end": v(36.8, 0) * mm});
            skArc(sketch, "E10.27.9", {"start": v(36.8, 0) * mm, "mid": v(36.22, -0.24) * mm, "end": v(35.97, -0.8) * mm});
            skArc(sketch, "E10.28.0", {"start": v(34.54, 10.1) * mm, "mid": v(34.93, 9.6) * mm, "end": v(35.55, 9.52) * mm});
            skLineSegment(sketch, "E10.28.1", {"start": v(36.8, 9.86) * mm, "end": v(35.55, 9.52) * mm});
            skArc(sketch, "E10.28.2", {"start": v(36.8, 9.86) * mm, "mid": v(37.74, 9.71) * mm, "end": v(38.66, 9.47) * mm});
            skArc(sketch, "E10.28.3", {"start": v(39.22, 8.86) * mm, "mid": v(39.03, 9.24) * mm, "end": v(38.66, 9.47) * mm});
            skLineSegment(sketch, "E10.28.4", {"start": v(39.22, 8.86) * mm, "end": v(39.26, 8.7) * mm});
            skLineSegment(sketch, "E10.28.5", {"start": v(39.3, 8.54) * mm, "end": v(39.26, 8.7) * mm});
            skArc(sketch, "E10.28.6", {"start": v(39.05, 7.76) * mm, "mid": v(39.28, 8.12) * mm, "end": v(39.3, 8.54) * mm});
            skArc(sketch, "E10.28.7", {"start": v(37.52, 6.62) * mm, "mid": v(38.31, 7.15) * mm, "end": v(39.05, 7.76) * mm});
            skLineSegment(sketch, "E10.28.8", {"start": v(37.52, 6.62) * mm, "end": v(36.24, 6.4) * mm});
            skArc(sketch, "E10.28.9", {"start": v(36.24, 6.4) * mm, "mid": v(35.71, 6.06) * mm, "end": v(35.57, 5.45) * mm});
            skArc(sketch, "E10.29.0", {"start": v(32.26, 15.93) * mm, "mid": v(32.73, 15.52) * mm, "end": v(33.35, 15.55) * mm});
            skLineSegment(sketch, "E10.29.1", {"start": v(34.53, 16.1) * mm, "end": v(33.35, 15.55) * mm});
            skArc(sketch, "E10.29.2", {"start": v(34.53, 16.1) * mm, "mid": v(35.48, 16.12) * mm, "end": v(36.43, 16.04) * mm});
            skArc(sketch, "E10.29.3", {"start": v(37.09, 15.54) * mm, "mid": v(36.83, 15.88) * mm, "end": v(36.43, 16.04) * mm});
            skLineSegment(sketch, "E10.29.4", {"start": v(37.09, 15.54) * mm, "end": v(37.15, 15.39) * mm});
            skLineSegment(sketch, "E10.29.5", {"start": v(37.21, 15.24) * mm, "end": v(37.15, 15.39) * mm});
            skArc(sketch, "E10.29.6", {"start": v(37.1, 14.42) * mm, "mid": v(37.27, 14.81) * mm, "end": v(37.21, 15.24) * mm});
            skArc(sketch, "E10.29.7", {"start": v(35.8, 13.03) * mm, "mid": v(36.49, 13.7) * mm, "end": v(37.1, 14.42) * mm});
            skLineSegment(sketch, "E10.29.8", {"start": v(35.8, 13.03) * mm, "end": v(34.58, 12.59) * mm});
            skArc(sketch, "E10.29.9", {"start": v(34.58, 12.59) * mm, "mid": v(34.12, 12.17) * mm, "end": v(34.08, 11.55) * mm});
            skArc(sketch, "E10.30.0", {"start": v(29, 21.3) * mm, "mid": v(29.54, 20.97) * mm, "end": v(30.14, 21.1) * mm});
            skLineSegment(sketch, "E10.30.1", {"start": v(31.2, 21.85) * mm, "end": v(30.14, 21.1) * mm});
            skArc(sketch, "E10.30.2", {"start": v(31.2, 21.85) * mm, "mid": v(32.14, 22.04) * mm, "end": v(33.1, 22.13) * mm});
            skArc(sketch, "E10.30.3", {"start": v(33.83, 21.74) * mm, "mid": v(33.51, 22.03) * mm, "end": v(33.1, 22.13) * mm});
            skLineSegment(sketch, "E10.30.4", {"start": v(33.83, 21.74) * mm, "end": v(33.91, 21.6) * mm});
            skLineSegment(sketch, "E10.30.5", {"start": v(34, 21.47) * mm, "end": v(33.91, 21.6) * mm});
            skArc(sketch, "E10.30.6", {"start": v(34.04, 20.64) * mm, "mid": v(34.13, 21.06) * mm, "end": v(34, 21.47) * mm});
            skArc(sketch, "E10.30.7", {"start": v(33, 19.05) * mm, "mid": v(33.56, 19.82) * mm, "end": v(34.04, 20.64) * mm});
            skArc(sketch, "E10.30.9", {"start": v(31.87, 18.4) * mm, "mid": v(31.49, 17.9) * mm, "end": v(31.56, 17.29) * mm});
            skArc(sketch, "E10.31.0", {"start": v(24.87, 26) * mm, "mid": v(25.45, 25.78) * mm, "end": v(26.02, 26.02) * mm});
            skLineSegment(sketch, "E10.31.1", {"start": v(26.94, 26.94) * mm, "end": v(26.02, 26.02) * mm});
            skArc(sketch, "E10.31.2", {"start": v(26.94, 26.94) * mm, "mid": v(27.83, 27.28) * mm, "end": v(28.75, 27.54) * mm});
            skArc(sketch, "E10.31.3", {"start": v(29.54, 27.29) * mm, "mid": v(29.18, 27.52) * mm, "end": v(28.75, 27.54) * mm});
            skLineSegment(sketch, "E10.31.4", {"start": v(29.54, 27.29) * mm, "end": v(29.65, 27.17) * mm});
            skLineSegment(sketch, "E10.31.5", {"start": v(29.76, 27.05) * mm, "end": v(29.65, 27.17) * mm});
            skArc(sketch, "E10.31.6", {"start": v(29.94, 26.24) * mm, "mid": v(29.96, 26.67) * mm, "end": v(29.76, 27.05) * mm});
            skArc(sketch, "E10.31.7", {"start": v(29.19, 24.5) * mm, "mid": v(29.6, 25.35) * mm, "end": v(29.94, 26.24) * mm});
            skLineSegment(sketch, "E10.31.8", {"start": v(29.19, 24.5) * mm, "end": v(28.2, 23.65) * mm});
            skArc(sketch, "E10.31.9", {"start": v(28.2, 23.65) * mm, "mid": v(27.9, 23.1) * mm, "end": v(28.08, 22.5) * mm});
            skArc(sketch, "E10.32.0", {"start": v(19.97, 29.93) * mm, "mid": v(20.58, 29.8) * mm, "end": v(21.1, 30.14) * mm});
            skLineSegment(sketch, "E10.32.1", {"start": v(21.85, 31.2) * mm, "end": v(21.1, 30.14) * mm});
            skArc(sketch, "E10.32.2", {"start": v(21.85, 31.2) * mm, "mid": v(22.67, 31.7) * mm, "end": v(23.53, 32.1) * mm});
            skArc(sketch, "E10.32.3", {"start": v(24.35, 32) * mm, "mid": v(23.95, 32.17) * mm, "end": v(23.53, 32.1) * mm});
            skLineSegment(sketch, "E10.32.4", {"start": v(24.35, 32) * mm, "end": v(24.48, 31.9) * mm});
            skLineSegment(sketch, "E10.32.5", {"start": v(24.6, 31.8) * mm, "end": v(24.48, 31.9) * mm});
            skArc(sketch, "E10.32.6", {"start": v(24.93, 31.04) * mm, "mid": v(24.87, 31.46) * mm, "end": v(24.6, 31.8) * mm});
            skArc(sketch, "E10.32.7", {"start": v(24.5, 29.19) * mm, "mid": v(24.75, 30.1) * mm, "end": v(24.93, 31.04) * mm});
            skLineSegment(sketch, "E10.32.8", {"start": v(24.5, 29.19) * mm, "end": v(23.65, 28.2) * mm});
            skArc(sketch, "E10.32.9", {"start": v(23.65, 28.2) * mm, "mid": v(23.46, 27.6) * mm, "end": v(23.74, 27.04) * mm});
            skArc(sketch, "E10.33.0", {"start": v(14.47, 32.94) * mm, "mid": v(15.1, 32.93) * mm, "end": v(15.55, 33.35) * mm});
            skLineSegment(sketch, "E10.33.1", {"start": v(16.1, 34.53) * mm, "end": v(15.55, 33.35) * mm});
            skArc(sketch, "E10.33.2", {"start": v(16.1, 34.53) * mm, "mid": v(16.82, 35.16) * mm, "end": v(17.6, 35.7) * mm});
            skArc(sketch, "E10.33.3", {"start": v(18.42, 35.74) * mm, "mid": v(18, 35.84) * mm, "end": v(17.6, 35.7) * mm});
            skLineSegment(sketch, "E10.33.4", {"start": v(18.42, 35.74) * mm, "end": v(18.57, 35.67) * mm});
            skLineSegment(sketch, "E10.33.5", {"start": v(18.71, 35.6) * mm, "end": v(18.57, 35.67) * mm});
            skArc(sketch, "E10.33.6", {"start": v(19.16, 34.9) * mm, "mid": v(19.03, 35.3) * mm, "end": v(18.71, 35.6) * mm});
            skArc(sketch, "E10.33.7", {"start": v(19.05, 33) * mm, "mid": v(19.15, 33.94) * mm, "end": v(19.16, 34.9) * mm});
            skLineSegment(sketch, "E10.33.8", {"start": v(19.05, 33) * mm, "end": v(18.4, 31.87) * mm});
            skArc(sketch, "E10.33.9", {"start": v(18.4, 31.87) * mm, "mid": v(18.31, 31.25) * mm, "end": v(18.69, 30.75) * mm});
            skArc(sketch, "E10.34.0", {"start": v(8.53, 34.96) * mm, "mid": v(9.15, 35.05) * mm, "end": v(9.52, 35.55) * mm});
            skLineSegment(sketch, "E10.34.1", {"start": v(9.86, 36.8) * mm, "end": v(9.52, 35.55) * mm});
            skArc(sketch, "E10.34.2", {"start": v(9.86, 36.8) * mm, "mid": v(10.46, 37.54) * mm, "end": v(11.13, 38.22) * mm});
            skArc(sketch, "E10.34.3", {"start": v(11.93, 38.4) * mm, "mid": v(11.5, 38.42) * mm, "end": v(11.13, 38.22) * mm});
            skLineSegment(sketch, "E10.34.4", {"start": v(11.93, 38.4) * mm, "end": v(12.1, 38.35) * mm});
            skLineSegment(sketch, "E10.34.5", {"start": v(12.25, 38.3) * mm, "end": v(12.1, 38.35) * mm});
            skArc(sketch, "E10.34.6", {"start": v(12.8, 37.7) * mm, "mid": v(12.6, 38.07) * mm, "end": v(12.25, 38.3) * mm});
            skArc(sketch, "E10.34.7", {"start": v(13.03, 35.8) * mm, "mid": v(12.97, 36.75) * mm, "end": v(12.8, 37.7) * mm});
            skLineSegment(sketch, "E10.34.8", {"start": v(13.03, 35.8) * mm, "end": v(12.59, 34.58) * mm});
            skArc(sketch, "E10.34.9", {"start": v(12.59, 34.58) * mm, "mid": v(12.6, 33.96) * mm, "end": v(13.06, 33.53) * mm});
            skArc(sketch, "E10.35.0", {"start": v(2.33, 35.9) * mm, "mid": v(2.92, 36.1) * mm, "end": v(3.2, 36.66) * mm});
            skLineSegment(sketch, "E10.35.1", {"start": v(3.32, 37.96) * mm, "end": v(3.2, 36.66) * mm});
            skArc(sketch, "E10.35.2", {"start": v(3.32, 37.96) * mm, "mid": v(3.78, 38.79) * mm, "end": v(4.32, 39.57) * mm});
            skArc(sketch, "E10.35.3", {"start": v(5.09, 39.89) * mm, "mid": v(4.66, 39.83) * mm, "end": v(4.32, 39.57) * mm});
            skLineSegment(sketch, "E10.35.4", {"start": v(5.09, 39.89) * mm, "end": v(5.25, 39.87) * mm});
            skLineSegment(sketch, "E10.35.5", {"start": v(5.41, 39.85) * mm, "end": v(5.25, 39.87) * mm});
            skArc(sketch, "E10.35.6", {"start": v(6.07, 39.34) * mm, "mid": v(5.8, 39.68) * mm, "end": v(5.41, 39.85) * mm});
            skArc(sketch, "E10.35.7", {"start": v(6.62, 37.52) * mm, "mid": v(6.39, 38.45) * mm, "end": v(6.07, 39.34) * mm});
            skLineSegment(sketch, "E10.35.8", {"start": v(6.62, 37.52) * mm, "end": v(6.4, 36.24) * mm});
            skArc(sketch, "E10.35.9", {"start": v(6.4, 36.24) * mm, "mid": v(6.52, 35.63) * mm, "end": v(7.04, 35.29) * mm});
            skPoint(sketch, "E10.center", {"position": v(0, 0) * mm});
            skArc(sketch, "E11.trimOffspring", {"start": v(-15.93, 32.26) * mm, "mid": v(-16.62, 31.92) * mm, "end": v(-17.29, 31.56) * mm});
            skArc(sketch, "E12.trimOffspring", {"start": v(-10.1, 34.54) * mm, "mid": v(-10.82, 34.32) * mm, "end": v(-11.55, 34.08) * mm});
            skArc(sketch, "E13.trimOffspring", {"start": v(2.33, 35.9) * mm, "mid": v(1.57, 35.95) * mm, "end": v(0.8, 35.97) * mm});
            skArc(sketch, "E14.trimOffspring", {"start": v(8.53, 34.96) * mm, "mid": v(7.79, 35.13) * mm, "end": v(7.04, 35.29) * mm});
            skArc(sketch, "E15.trimOffspring", {"start": v(14.47, 32.94) * mm, "mid": v(13.77, 33.24) * mm, "end": v(13.06, 33.53) * mm});
            skArc(sketch, "E16.trimOffspring", {"start": v(19.97, 29.93) * mm, "mid": v(19.33, 30.35) * mm, "end": v(18.69, 30.75) * mm});
            skArc(sketch, "E17.trimOffspring", {"start": v(-29, -21.3) * mm, "mid": v(-28.55, -21.9) * mm, "end": v(-28.08, -22.5) * mm});
            skArc(sketch, "E18.trimOffspring", {"start": v(-32.26, -15.93) * mm, "mid": v(-31.92, -16.62) * mm, "end": v(-31.56, -17.29) * mm});
            skArc(sketch, "E19.trimOffspring", {"start": v(-34.54, -10.1) * mm, "mid": v(-34.32, -10.82) * mm, "end": v(-34.08, -11.55) * mm});
            skArc(sketch, "E20.trimOffspring", {"start": v(-35.77, -3.94) * mm, "mid": v(-35.68, -4.7) * mm, "end": v(-35.57, -5.45) * mm});
            skArc(sketch, "E21.trimOffspring", {"start": v(-19.97, -29.93) * mm, "mid": v(-19.33, -30.35) * mm, "end": v(-18.69, -30.75) * mm});
            skArc(sketch, "E22.trimOffspring", {"start": v(29.93, -19.97) * mm, "mid": v(30.35, -19.33) * mm, "end": v(30.75, -18.69) * mm});
            skArc(sketch, "E23.trimOffspring", {"start": v(26, -24.87) * mm, "mid": v(26.53, -24.3) * mm, "end": v(27.04, -23.74) * mm});
            skArc(sketch, "E24.trimOffspring", {"start": v(21.3, -29) * mm, "mid": v(21.9, -28.55) * mm, "end": v(22.5, -28.08) * mm});
            skArc(sketch, "E25.trimOffspring", {"start": v(15.93, -32.26) * mm, "mid": v(16.62, -31.92) * mm, "end": v(17.29, -31.56) * mm});
            skArc(sketch, "E26.trimOffspring", {"start": v(34.96, -8.53) * mm, "mid": v(35.13, -7.79) * mm, "end": v(35.29, -7.04) * mm});
            skArc(sketch, "E27.trimOffspring", {"start": v(32.94, -14.47) * mm, "mid": v(33.24, -13.77) * mm, "end": v(33.53, -13.06) * mm});
            skArc(sketch, "E28.trimOffspring", {"start": v(35.77, 3.94) * mm, "mid": v(35.68, 4.7) * mm, "end": v(35.57, 5.45) * mm});
            skArc(sketch, "E29.trimOffspring", {"start": v(-35.9, 2.33) * mm, "mid": v(-35.95, 1.57) * mm, "end": v(-35.97, 0.8) * mm});
            skArc(sketch, "E30.trimOffspring", {"start": v(-34.96, 8.53) * mm, "mid": v(-35.13, 7.79) * mm, "end": v(-35.29, 7.04) * mm});
            skArc(sketch, "E31.trimOffspring", {"start": v(-32.94, 14.47) * mm, "mid": v(-33.24, 13.77) * mm, "end": v(-33.53, 13.06) * mm});
            skArc(sketch, "E32.trimOffspring", {"start": v(-29.93, 19.97) * mm, "mid": v(-30.35, 19.33) * mm, "end": v(-30.75, 18.69) * mm});
            skArc(sketch, "E33.trimOffspring", {"start": v(-26, 24.87) * mm, "mid": v(-26.53, 24.3) * mm, "end": v(-27.04, 23.74) * mm});
            skArc(sketch, "E34.trimOffspring", {"start": v(-21.3, 29) * mm, "mid": v(-21.9, 28.55) * mm, "end": v(-22.5, 28.08) * mm});
            skArc(sketch, "E35.trimOffspring", {"start": v(24.87, 26) * mm, "mid": v(24.3, 26.53) * mm, "end": v(23.74, 27.04) * mm});
            skArc(sketch, "E36.trimOffspring", {"start": v(32.26, 15.93) * mm, "mid": v(31.92, 16.62) * mm, "end": v(31.56, 17.29) * mm});
            skArc(sketch, "E37.trimOffspring", {"start": v(34.54, 10.1) * mm, "mid": v(34.32, 10.82) * mm, "end": v(34.08, 11.55) * mm});
            skArc(sketch, "E38.trimOffspring", {"start": v(29, 21.3) * mm, "mid": v(28.55, 21.9) * mm, "end": v(28.08, 22.5) * mm});
            skLineSegment(sketch, "E39", {"start": v(31.87, 18.4) * mm, "end": v(33, 19.05) * mm});
            skArc(sketch, "E40.trimOffspring", {"start": v(3.94, -35.77) * mm, "mid": v(4.7, -35.68) * mm, "end": v(5.45, -35.57) * mm});
            skLineSegment(sketch, "E41", {"start": v(-24.87, -26) * mm, "end": v(-23.74, -27.04) * mm});
            skLineSegment(sketch, "E42", {"start": v(-14.47, -32.94) * mm, "end": v(-13.06, -33.53) * mm});
            skLineSegment(sketch, "E43", {"start": v(-8.53, -34.96) * mm, "end": v(-7.04, -35.29) * mm});
            skLineSegment(sketch, "E44", {"start": v(-2.33, -35.9) * mm, "end": v(-0.8, -35.97) * mm});
            skLineSegment(sketch, "E45", {"start": v(10.1, -34.54) * mm, "end": v(11.55, -34.08) * mm});
            skLineSegment(sketch, "E46", {"start": v(-5.45, 35.57) * mm, "end": v(-3.94, 35.77) * mm});
            skLineSegment(sketch, "E47", {"start": v(35.9, -2.33) * mm, "end": v(35.97, -0.8) * mm});
            skSolve(sketch);
        }
        {
            var Q0;
            Q0 = qSketchRegion(id + "F0", true);
            extrude(context, id + "F1", {"entities" : qUnion([Q0]), "depth" : 12.7 * mm});
        }
        {
            var Q0;
            Q0=makeQuery(id+"F1.opExtrude","CAP_FACE",FACE,{"disambiguationData":[OSD([sQuery(id+"F0.wireOp",EDGE,"E0.trimOffspring"),sQuery(id+"F0.wireOp",EDGE,"E1"),sQuery(id+"F0.wireOp",EDGE,"E2"),sQuery(id+"F0.wireOp",EDGE,"E3.MirrorCS"),sQuery(id+"F0.wireOp",EDGE,"E4.MirrorCS"),sQuery(id+"F0.wireOp",EDGE,"E5.MirrorCS"),sQuery(id+"F0.wireOp",EDGE,"E6.filletArc"),sQuery(id+"F0.wireOp",EDGE,"E7.filletArc"),sQuery(id+"F0.wireOp",EDGE,"E8.filletArc"),sQuery(id+"F0.wireOp",EDGE,"E9.filletArc"),sQuery(id+"F0.wireOp",EDGE,"E10.1.0"),sQuery(id+"F0.wireOp",EDGE,"E10.1.1"),sQuery(id+"F0.wireOp",EDGE,"E10.1.2"),sQuery(id+"F0.wireOp",EDGE,"E10.1.3"),sQuery(id+"F0.wireOp",EDGE,"E10.1.4"),sQuery(id+"F0.wireOp",EDGE,"E10.1.5"),sQuery(id+"F0.wireOp",EDGE,"E10.1.6"),sQuery(id+"F0.wireOp",EDGE,"E10.1.7"),sQuery(id+"F0.wireOp",EDGE,"E10.1.8"),sQuery(id+"F0.wireOp",EDGE,"E10.1.9"),sQuery(id+"F0.wireOp",EDGE,"E10.2.0"),sQuery(id+"F0.wireOp",EDGE,"E10.2.1"),sQuery(id+"F0.wireOp",EDGE,"E10.2.2"),sQuery(id+"F0.wireOp",EDGE,"E10.2.3"),sQuery(id+"F0.wireOp",EDGE,"E10.2.4"),sQuery(id+"F0.wireOp",EDGE,"E10.2.5"),sQuery(id+"F0.wireOp",EDGE,"E10.2.6"),sQuery(id+"F0.wireOp",EDGE,"E10.2.7"),sQuery(id+"F0.wireOp",EDGE,"E10.2.8"),sQuery(id+"F0.wireOp",EDGE,"E10.2.9"),sQuery(id+"F0.wireOp",EDGE,"E10.3.0"),sQuery(id+"F0.wireOp",EDGE,"E10.3.1"),sQuery(id+"F0.wireOp",EDGE,"E10.3.2"),sQuery(id+"F0.wireOp",EDGE,"E10.3.3"),sQuery(id+"F0.wireOp",EDGE,"E10.3.4"),sQuery(id+"F0.wireOp",EDGE,"E10.3.5"),sQuery(id+"F0.wireOp",EDGE,"E10.3.6"),sQuery(id+"F0.wireOp",EDGE,"E10.3.7"),sQuery(id+"F0.wireOp",EDGE,"E10.3.8"),sQuery(id+"F0.wireOp",EDGE,"E10.3.9"),sQuery(id+"F0.wireOp",EDGE,"E10.4.0"),sQuery(id+"F0.wireOp",EDGE,"E10.4.1"),sQuery(id+"F0.wireOp",EDGE,"E10.4.2"),sQuery(id+"F0.wireOp",EDGE,"E10.4.3"),sQuery(id+"F0.wireOp",EDGE,"E10.4.4"),sQuery(id+"F0.wireOp",EDGE,"E10.4.5"),sQuery(id+"F0.wireOp",EDGE,"E10.4.6"),sQuery(id+"F0.wireOp",EDGE,"E10.4.7"),sQuery(id+"F0.wireOp",EDGE,"E10.4.8"),sQuery(id+"F0.wireOp",EDGE,"E10.4.9"),sQuery(id+"F0.wireOp",EDGE,"E10.5.0"),sQuery(id+"F0.wireOp",EDGE,"E10.5.1"),sQuery(id+"F0.wireOp",EDGE,"E10.5.2"),sQuery(id+"F0.wireOp",EDGE,"E10.5.3"),sQuery(id+"F0.wireOp",EDGE,"E10.5.4"),sQuery(id+"F0.wireOp",EDGE,"E10.5.5"),sQuery(id+"F0.wireOp",EDGE,"E10.5.6"),sQuery(id+"F0.wireOp",EDGE,"E10.5.7"),sQuery(id+"F0.wireOp",EDGE,"E10.5.8"),sQuery(id+"F0.wireOp",EDGE,"E10.5.9"),sQuery(id+"F0.wireOp",EDGE,"E10.6.0"),sQuery(id+"F0.wireOp",EDGE,"E10.6.1"),sQuery(id+"F0.wireOp",EDGE,"E10.6.2"),sQuery(id+"F0.wireOp",EDGE,"E10.6.3"),sQuery(id+"F0.wireOp",EDGE,"E10.6.4"),sQuery(id+"F0.wireOp",EDGE,"E10.6.5"),sQuery(id+"F0.wireOp",EDGE,"E10.6.6"),sQuery(id+"F0.wireOp",EDGE,"E10.6.7"),sQuery(id+"F0.wireOp",EDGE,"E10.6.8"),sQuery(id+"F0.wireOp",EDGE,"E10.6.9"),sQuery(id+"F0.wireOp",EDGE,"E10.7.0"),sQuery(id+"F0.wireOp",EDGE,"E10.7.1"),sQuery(id+"F0.wireOp",EDGE,"E10.7.2"),sQuery(id+"F0.wireOp",EDGE,"E10.7.3"),sQuery(id+"F0.wireOp",EDGE,"E10.7.4"),sQuery(id+"F0.wireOp",EDGE,"E10.7.5"),sQuery(id+"F0.wireOp",EDGE,"E10.7.6"),sQuery(id+"F0.wireOp",EDGE,"E10.7.7"),sQuery(id+"F0.wireOp",EDGE,"E10.7.8"),sQuery(id+"F0.wireOp",EDGE,"E10.7.9"),sQuery(id+"F0.wireOp",EDGE,"E10.8.0"),sQuery(id+"F0.wireOp",EDGE,"E10.8.1"),sQuery(id+"F0.wireOp",EDGE,"E10.8.2"),sQuery(id+"F0.wireOp",EDGE,"E10.8.3"),sQuery(id+"F0.wireOp",EDGE,"E10.8.4"),sQuery(id+"F0.wireOp",EDGE,"E10.8.5"),sQuery(id+"F0.wireOp",EDGE,"E10.8.6"),sQuery(id+"F0.wireOp",EDGE,"E10.8.7"),sQuery(id+"F0.wireOp",EDGE,"E10.8.8"),sQuery(id+"F0.wireOp",EDGE,"E10.8.9"),sQuery(id+"F0.wireOp",EDGE,"E10.9.0"),sQuery(id+"F0.wireOp",EDGE,"E10.9.1"),sQuery(id+"F0.wireOp",EDGE,"E10.9.2"),sQuery(id+"F0.wireOp",EDGE,"E10.9.3"),sQuery(id+"F0.wireOp",EDGE,"E10.9.4"),sQuery(id+"F0.wireOp",EDGE,"E10.9.5"),sQuery(id+"F0.wireOp",EDGE,"E10.9.6"),sQuery(id+"F0.wireOp",EDGE,"E10.9.7"),sQuery(id+"F0.wireOp",EDGE,"E10.9.8"),sQuery(id+"F0.wireOp",EDGE,"E10.9.9"),sQuery(id+"F0.wireOp",EDGE,"E10.10.0"),sQuery(id+"F0.wireOp",EDGE,"E10.10.1"),sQuery(id+"F0.wireOp",EDGE,"E10.10.2"),sQuery(id+"F0.wireOp",EDGE,"E10.10.3"),sQuery(id+"F0.wireOp",EDGE,"E10.10.4"),sQuery(id+"F0.wireOp",EDGE,"E10.10.5"),sQuery(id+"F0.wireOp",EDGE,"E10.10.6"),sQuery(id+"F0.wireOp",EDGE,"E10.10.7"),sQuery(id+"F0.wireOp",EDGE,"E10.10.8"),sQuery(id+"F0.wireOp",EDGE,"E10.10.9"),sQuery(id+"F0.wireOp",EDGE,"E10.11.0"),sQuery(id+"F0.wireOp",EDGE,"E10.11.1"),sQuery(id+"F0.wireOp",EDGE,"E10.11.2"),sQuery(id+"F0.wireOp",EDGE,"E10.11.3"),sQuery(id+"F0.wireOp",EDGE,"E10.11.4"),sQuery(id+"F0.wireOp",EDGE,"E10.11.5"),sQuery(id+"F0.wireOp",EDGE,"E10.11.6"),sQuery(id+"F0.wireOp",EDGE,"E10.11.7"),sQuery(id+"F0.wireOp",EDGE,"E10.11.8"),sQuery(id+"F0.wireOp",EDGE,"E10.11.9"),sQuery(id+"F0.wireOp",EDGE,"E10.12.0"),sQuery(id+"F0.wireOp",EDGE,"E10.12.1"),sQuery(id+"F0.wireOp",EDGE,"E10.12.2"),sQuery(id+"F0.wireOp",EDGE,"E10.12.3"),sQuery(id+"F0.wireOp",EDGE,"E10.12.4"),sQuery(id+"F0.wireOp",EDGE,"E10.12.5"),sQuery(id+"F0.wireOp",EDGE,"E10.12.6"),sQuery(id+"F0.wireOp",EDGE,"E10.12.7"),sQuery(id+"F0.wireOp",EDGE,"E10.12.8"),sQuery(id+"F0.wireOp",EDGE,"E10.12.9"),sQuery(id+"F0.wireOp",EDGE,"E10.13.0"),sQuery(id+"F0.wireOp",EDGE,"E10.13.1"),sQuery(id+"F0.wireOp",EDGE,"E10.13.2"),sQuery(id+"F0.wireOp",EDGE,"E10.13.3"),sQuery(id+"F0.wireOp",EDGE,"E10.13.4"),sQuery(id+"F0.wireOp",EDGE,"E10.13.5"),sQuery(id+"F0.wireOp",EDGE,"E10.13.6"),sQuery(id+"F0.wireOp",EDGE,"E10.13.7"),sQuery(id+"F0.wireOp",EDGE,"E10.13.8"),sQuery(id+"F0.wireOp",EDGE,"E10.13.9"),sQuery(id+"F0.wireOp",EDGE,"E10.14.0"),sQuery(id+"F0.wireOp",EDGE,"E10.14.1"),sQuery(id+"F0.wireOp",EDGE,"E10.14.2"),sQuery(id+"F0.wireOp",EDGE,"E10.14.3"),sQuery(id+"F0.wireOp",EDGE,"E10.14.4"),sQuery(id+"F0.wireOp",EDGE,"E10.14.5"),sQuery(id+"F0.wireOp",EDGE,"E10.14.6"),sQuery(id+"F0.wireOp",EDGE,"E10.14.7"),sQuery(id+"F0.wireOp",EDGE,"E10.14.8"),sQuery(id+"F0.wireOp",EDGE,"E10.14.9"),sQuery(id+"F0.wireOp",EDGE,"E10.15.0"),sQuery(id+"F0.wireOp",EDGE,"E10.15.1"),sQuery(id+"F0.wireOp",EDGE,"E10.15.2"),sQuery(id+"F0.wireOp",EDGE,"E10.15.3"),sQuery(id+"F0.wireOp",EDGE,"E10.15.4"),sQuery(id+"F0.wireOp",EDGE,"E10.15.5"),sQuery(id+"F0.wireOp",EDGE,"E10.15.6"),sQuery(id+"F0.wireOp",EDGE,"E10.15.7"),sQuery(id+"F0.wireOp",EDGE,"E10.15.8"),sQuery(id+"F0.wireOp",EDGE,"E10.15.9"),sQuery(id+"F0.wireOp",EDGE,"E10.16.0"),sQuery(id+"F0.wireOp",EDGE,"E10.16.1"),sQuery(id+"F0.wireOp",EDGE,"E10.16.2"),sQuery(id+"F0.wireOp",EDGE,"E10.16.3"),sQuery(id+"F0.wireOp",EDGE,"E10.16.4"),sQuery(id+"F0.wireOp",EDGE,"E10.16.5"),sQuery(id+"F0.wireOp",EDGE,"E10.16.6"),sQuery(id+"F0.wireOp",EDGE,"E10.16.7"),sQuery(id+"F0.wireOp",EDGE,"E10.16.8"),sQuery(id+"F0.wireOp",EDGE,"E10.16.9"),sQuery(id+"F0.wireOp",EDGE,"E10.17.0"),sQuery(id+"F0.wireOp",EDGE,"E10.17.1"),sQuery(id+"F0.wireOp",EDGE,"E10.17.2"),sQuery(id+"F0.wireOp",EDGE,"E10.17.3"),sQuery(id+"F0.wireOp",EDGE,"E10.17.4"),sQuery(id+"F0.wireOp",EDGE,"E10.17.5"),sQuery(id+"F0.wireOp",EDGE,"E10.17.6"),sQuery(id+"F0.wireOp",EDGE,"E10.17.7"),sQuery(id+"F0.wireOp",EDGE,"E10.17.8"),sQuery(id+"F0.wireOp",EDGE,"E10.17.9"),sQuery(id+"F0.wireOp",EDGE,"E10.18.0"),sQuery(id+"F0.wireOp",EDGE,"E10.18.1"),sQuery(id+"F0.wireOp",EDGE,"E10.18.2"),sQuery(id+"F0.wireOp",EDGE,"E10.18.3"),sQuery(id+"F0.wireOp",EDGE,"E10.18.4"),sQuery(id+"F0.wireOp",EDGE,"E10.18.5"),sQuery(id+"F0.wireOp",EDGE,"E10.18.6"),sQuery(id+"F0.wireOp",EDGE,"E10.18.7"),sQuery(id+"F0.wireOp",EDGE,"E10.18.8"),sQuery(id+"F0.wireOp",EDGE,"E10.18.9"),sQuery(id+"F0.wireOp",EDGE,"E10.19.0"),sQuery(id+"F0.wireOp",EDGE,"E10.19.1"),sQuery(id+"F0.wireOp",EDGE,"E10.19.2"),sQuery(id+"F0.wireOp",EDGE,"E10.19.3"),sQuery(id+"F0.wireOp",EDGE,"E10.19.4"),sQuery(id+"F0.wireOp",EDGE,"E10.19.5"),sQuery(id+"F0.wireOp",EDGE,"E10.19.6"),sQuery(id+"F0.wireOp",EDGE,"E10.19.7"),sQuery(id+"F0.wireOp",EDGE,"E10.19.8"),sQuery(id+"F0.wireOp",EDGE,"E10.19.9"),sQuery(id+"F0.wireOp",EDGE,"E10.20.0"),sQuery(id+"F0.wireOp",EDGE,"E10.20.1"),sQuery(id+"F0.wireOp",EDGE,"E10.20.2"),sQuery(id+"F0.wireOp",EDGE,"E10.20.3"),sQuery(id+"F0.wireOp",EDGE,"E10.20.4"),sQuery(id+"F0.wireOp",EDGE,"E10.20.5"),sQuery(id+"F0.wireOp",EDGE,"E10.20.6"),sQuery(id+"F0.wireOp",EDGE,"E10.20.7"),sQuery(id+"F0.wireOp",EDGE,"E10.20.8"),sQuery(id+"F0.wireOp",EDGE,"E10.20.9"),sQuery(id+"F0.wireOp",EDGE,"E10.21.0"),sQuery(id+"F0.wireOp",EDGE,"E10.21.1"),sQuery(id+"F0.wireOp",EDGE,"E10.21.2"),sQuery(id+"F0.wireOp",EDGE,"E10.21.3"),sQuery(id+"F0.wireOp",EDGE,"E10.21.4"),sQuery(id+"F0.wireOp",EDGE,"E10.21.5"),sQuery(id+"F0.wireOp",EDGE,"E10.21.6"),sQuery(id+"F0.wireOp",EDGE,"E10.21.7"),sQuery(id+"F0.wireOp",EDGE,"E10.21.8"),sQuery(id+"F0.wireOp",EDGE,"E10.21.9"),sQuery(id+"F0.wireOp",EDGE,"E10.22.0"),sQuery(id+"F0.wireOp",EDGE,"E10.22.1"),sQuery(id+"F0.wireOp",EDGE,"E10.22.2"),sQuery(id+"F0.wireOp",EDGE,"E10.22.3"),sQuery(id+"F0.wireOp",EDGE,"E10.22.4"),sQuery(id+"F0.wireOp",EDGE,"E10.22.5"),sQuery(id+"F0.wireOp",EDGE,"E10.22.6"),sQuery(id+"F0.wireOp",EDGE,"E10.22.7"),sQuery(id+"F0.wireOp",EDGE,"E10.22.8"),sQuery(id+"F0.wireOp",EDGE,"E10.22.9"),sQuery(id+"F0.wireOp",EDGE,"E10.23.0"),sQuery(id+"F0.wireOp",EDGE,"E10.23.1"),sQuery(id+"F0.wireOp",EDGE,"E10.23.2"),sQuery(id+"F0.wireOp",EDGE,"E10.23.3"),sQuery(id+"F0.wireOp",EDGE,"E10.23.4"),sQuery(id+"F0.wireOp",EDGE,"E10.23.5"),sQuery(id+"F0.wireOp",EDGE,"E10.23.6"),sQuery(id+"F0.wireOp",EDGE,"E10.23.7"),sQuery(id+"F0.wireOp",EDGE,"E10.23.8"),sQuery(id+"F0.wireOp",EDGE,"E10.23.9"),sQuery(id+"F0.wireOp",EDGE,"E10.24.0"),sQuery(id+"F0.wireOp",EDGE,"E10.24.1"),sQuery(id+"F0.wireOp",EDGE,"E10.24.2"),sQuery(id+"F0.wireOp",EDGE,"E10.24.3"),sQuery(id+"F0.wireOp",EDGE,"E10.24.4"),sQuery(id+"F0.wireOp",EDGE,"E10.24.5"),sQuery(id+"F0.wireOp",EDGE,"E10.24.6"),sQuery(id+"F0.wireOp",EDGE,"E10.24.7"),sQuery(id+"F0.wireOp",EDGE,"E10.24.8"),sQuery(id+"F0.wireOp",EDGE,"E10.24.9"),sQuery(id+"F0.wireOp",EDGE,"E10.25.0"),sQuery(id+"F0.wireOp",EDGE,"E10.25.1"),sQuery(id+"F0.wireOp",EDGE,"E10.25.2"),sQuery(id+"F0.wireOp",EDGE,"E10.25.3"),sQuery(id+"F0.wireOp",EDGE,"E10.25.4"),sQuery(id+"F0.wireOp",EDGE,"E10.25.5"),sQuery(id+"F0.wireOp",EDGE,"E10.25.6"),sQuery(id+"F0.wireOp",EDGE,"E10.25.7"),sQuery(id+"F0.wireOp",EDGE,"E10.25.8"),sQuery(id+"F0.wireOp",EDGE,"E10.25.9"),sQuery(id+"F0.wireOp",EDGE,"E10.26.0"),sQuery(id+"F0.wireOp",EDGE,"E10.26.1"),sQuery(id+"F0.wireOp",EDGE,"E10.26.2"),sQuery(id+"F0.wireOp",EDGE,"E10.26.3"),sQuery(id+"F0.wireOp",EDGE,"E10.26.4"),sQuery(id+"F0.wireOp",EDGE,"E10.26.5"),sQuery(id+"F0.wireOp",EDGE,"E10.26.6"),sQuery(id+"F0.wireOp",EDGE,"E10.26.7"),sQuery(id+"F0.wireOp",EDGE,"E10.26.8"),sQuery(id+"F0.wireOp",EDGE,"E10.26.9"),sQuery(id+"F0.wireOp",EDGE,"E10.27.0"),sQuery(id+"F0.wireOp",EDGE,"E10.27.1"),sQuery(id+"F0.wireOp",EDGE,"E10.27.2"),sQuery(id+"F0.wireOp",EDGE,"E10.27.3"),sQuery(id+"F0.wireOp",EDGE,"E10.27.4"),sQuery(id+"F0.wireOp",EDGE,"E10.27.5"),sQuery(id+"F0.wireOp",EDGE,"E10.27.6"),sQuery(id+"F0.wireOp",EDGE,"E10.27.7"),sQuery(id+"F0.wireOp",EDGE,"E10.27.8"),sQuery(id+"F0.wireOp",EDGE,"E10.27.9"),sQuery(id+"F0.wireOp",EDGE,"E10.28.0"),sQuery(id+"F0.wireOp",EDGE,"E10.28.1"),sQuery(id+"F0.wireOp",EDGE,"E10.28.2"),sQuery(id+"F0.wireOp",EDGE,"E10.28.3"),sQuery(id+"F0.wireOp",EDGE,"E10.28.4"),sQuery(id+"F0.wireOp",EDGE,"E10.28.5"),sQuery(id+"F0.wireOp",EDGE,"E10.28.6"),sQuery(id+"F0.wireOp",EDGE,"E10.28.7"),sQuery(id+"F0.wireOp",EDGE,"E10.28.8"),sQuery(id+"F0.wireOp",EDGE,"E10.28.9"),sQuery(id+"F0.wireOp",EDGE,"E10.29.0"),sQuery(id+"F0.wireOp",EDGE,"E10.29.1"),sQuery(id+"F0.wireOp",EDGE,"E10.29.2"),sQuery(id+"F0.wireOp",EDGE,"E10.29.3"),sQuery(id+"F0.wireOp",EDGE,"E10.29.4"),sQuery(id+"F0.wireOp",EDGE,"E10.29.5"),sQuery(id+"F0.wireOp",EDGE,"E10.29.6"),sQuery(id+"F0.wireOp",EDGE,"E10.29.7"),sQuery(id+"F0.wireOp",EDGE,"E10.29.8"),sQuery(id+"F0.wireOp",EDGE,"E10.29.9"),sQuery(id+"F0.wireOp",EDGE,"E10.30.0"),sQuery(id+"F0.wireOp",EDGE,"E10.30.1"),sQuery(id+"F0.wireOp",EDGE,"E10.30.2"),sQuery(id+"F0.wireOp",EDGE,"E10.30.3"),sQuery(id+"F0.wireOp",EDGE,"E10.30.4"),sQuery(id+"F0.wireOp",EDGE,"E10.30.5"),sQuery(id+"F0.wireOp",EDGE,"E10.30.6"),sQuery(id+"F0.wireOp",EDGE,"E10.30.7"),sQuery(id+"F0.wireOp",EDGE,"E10.30.9"),sQuery(id+"F0.wireOp",EDGE,"E10.31.0"),sQuery(id+"F0.wireOp",EDGE,"E10.31.1"),sQuery(id+"F0.wireOp",EDGE,"E10.31.2"),sQuery(id+"F0.wireOp",EDGE,"E10.31.3"),sQuery(id+"F0.wireOp",EDGE,"E10.31.4"),sQuery(id+"F0.wireOp",EDGE,"E10.31.5"),sQuery(id+"F0.wireOp",EDGE,"E10.31.6"),sQuery(id+"F0.wireOp",EDGE,"E10.31.7"),sQuery(id+"F0.wireOp",EDGE,"E10.31.8"),sQuery(id+"F0.wireOp",EDGE,"E10.31.9"),sQuery(id+"F0.wireOp",EDGE,"E10.32.0"),sQuery(id+"F0.wireOp",EDGE,"E10.32.1"),sQuery(id+"F0.wireOp",EDGE,"E10.32.2"),sQuery(id+"F0.wireOp",EDGE,"E10.32.3"),sQuery(id+"F0.wireOp",EDGE,"E10.32.4"),sQuery(id+"F0.wireOp",EDGE,"E10.32.5"),sQuery(id+"F0.wireOp",EDGE,"E10.32.6"),sQuery(id+"F0.wireOp",EDGE,"E10.32.7"),sQuery(id+"F0.wireOp",EDGE,"E10.32.8"),sQuery(id+"F0.wireOp",EDGE,"E10.32.9"),sQuery(id+"F0.wireOp",EDGE,"E10.33.0"),sQuery(id+"F0.wireOp",EDGE,"E10.33.1"),sQuery(id+"F0.wireOp",EDGE,"E10.33.2"),sQuery(id+"F0.wireOp",EDGE,"E10.33.3"),sQuery(id+"F0.wireOp",EDGE,"E10.33.4"),sQuery(id+"F0.wireOp",EDGE,"E10.33.5"),sQuery(id+"F0.wireOp",EDGE,"E10.33.6"),sQuery(id+"F0.wireOp",EDGE,"E10.33.7"),sQuery(id+"F0.wireOp",EDGE,"E10.33.8"),sQuery(id+"F0.wireOp",EDGE,"E10.33.9"),sQuery(id+"F0.wireOp",EDGE,"E10.34.0"),sQuery(id+"F0.wireOp",EDGE,"E10.34.1"),sQuery(id+"F0.wireOp",EDGE,"E10.34.2"),sQuery(id+"F0.wireOp",EDGE,"E10.34.3"),sQuery(id+"F0.wireOp",EDGE,"E10.34.4"),sQuery(id+"F0.wireOp",EDGE,"E10.34.5"),sQuery(id+"F0.wireOp",EDGE,"E10.34.6"),sQuery(id+"F0.wireOp",EDGE,"E10.34.7"),sQuery(id+"F0.wireOp",EDGE,"E10.34.8"),sQuery(id+"F0.wireOp",EDGE,"E10.34.9"),sQuery(id+"F0.wireOp",EDGE,"E10.35.0"),sQuery(id+"F0.wireOp",EDGE,"E10.35.1"),sQuery(id+"F0.wireOp",EDGE,"E10.35.2"),sQuery(id+"F0.wireOp",EDGE,"E10.35.3"),sQuery(id+"F0.wireOp",EDGE,"E10.35.4"),sQuery(id+"F0.wireOp",EDGE,"E10.35.5"),sQuery(id+"F0.wireOp",EDGE,"E10.35.6"),sQuery(id+"F0.wireOp",EDGE,"E10.35.7"),sQuery(id+"F0.wireOp",EDGE,"E10.35.8"),sQuery(id+"F0.wireOp",EDGE,"E10.35.9"),sQuery(id+"F0.wireOp",EDGE,"E11.trimOffspring"),sQuery(id+"F0.wireOp",EDGE,"E12.trimOffspring"),sQuery(id+"F0.wireOp",EDGE,"E13.trimOffspring"),sQuery(id+"F0.wireOp",EDGE,"E14.trimOffspring"),sQuery(id+"F0.wireOp",EDGE,"E15.trimOffspring"),sQuery(id+"F0.wireOp",EDGE,"E16.trimOffspring"),sQuery(id+"F0.wireOp",EDGE,"E17.trimOffspring"),sQuery(id+"F0.wireOp",EDGE,"E18.trimOffspring"),sQuery(id+"F0.wireOp",EDGE,"E19.trimOffspring"),sQuery(id+"F0.wireOp",EDGE,"E20.trimOffspring"),sQuery(id+"F0.wireOp",EDGE,"E21.trimOffspring"),sQuery(id+"F0.wireOp",EDGE,"E22.trimOffspring"),sQuery(id+"F0.wireOp",EDGE,"E23.trimOffspring"),sQuery(id+"F0.wireOp",EDGE,"E24.trimOffspring"),sQuery(id+"F0.wireOp",EDGE,"E25.trimOffspring"),sQuery(id+"F0.wireOp",EDGE,"E26.trimOffspring"),sQuery(id+"F0.wireOp",EDGE,"E27.trimOffspring"),sQuery(id+"F0.wireOp",EDGE,"E28.trimOffspring"),sQuery(id+"F0.wireOp",EDGE,"E29.trimOffspring"),sQuery(id+"F0.wireOp",EDGE,"E30.trimOffspring"),sQuery(id+"F0.wireOp",EDGE,"E31.trimOffspring"),sQuery(id+"F0.wireOp",EDGE,"E32.trimOffspring"),sQuery(id+"F0.wireOp",EDGE,"E33.trimOffspring"),sQuery(id+"F0.wireOp",EDGE,"E34.trimOffspring"),sQuery(id+"F0.wireOp",EDGE,"E35.trimOffspring"),sQuery(id+"F0.wireOp",EDGE,"E36.trimOffspring"),sQuery(id+"F0.wireOp",EDGE,"E37.trimOffspring"),sQuery(id+"F0.wireOp",EDGE,"E38.trimOffspring"),sQuery(id+"F0.wireOp",EDGE,"E39"),sQuery(id+"F0.wireOp",EDGE,"E40.trimOffspring"),sQuery(id+"F0.wireOp",EDGE,"E41"),sQuery(id+"F0.wireOp",EDGE,"E42"),sQuery(id+"F0.wireOp",EDGE,"E43"),sQuery(id+"F0.wireOp",EDGE,"E44"),sQuery(id+"F0.wireOp",EDGE,"E45"),sQuery(id+"F0.wireOp",EDGE,"E46"),sQuery(id+"F0.wireOp",EDGE,"E47")])],"isStart":false});
            var sketch = newSketch(context, id + "F2", { "sketchPlane" : qUnion([Q0])});
            skCircle(sketch, "E48", {"center": v(0, 0) * mm, "radius": 3.18 * mm});
            skSolve(sketch);
        }
        {
            var Q0;
            Q0 = qSketchRegion(id + "F2", true);
            extrude(context, id + "F3", {"entities" : qUnion([Q0]), "operationType" : NewBodyOperationType.REMOVE, "endBound" : BoundingType.THROUGH_ALL, "oppositeDirection" : true, "depth" : 25.4 * mm});
        }
        {
            var Q0;
            Q0=makeQuery(id+"F1.opExtrude","CAP_FACE",FACE,{"disambiguationData":[OSD([sQuery(id+"F0.wireOp",EDGE,"E0.trimOffspring"),sQuery(id+"F0.wireOp",EDGE,"E1"),sQuery(id+"F0.wireOp",EDGE,"E2"),sQuery(id+"F0.wireOp",EDGE,"E3.MirrorCS"),sQuery(id+"F0.wireOp",EDGE,"E4.MirrorCS"),sQuery(id+"F0.wireOp",EDGE,"E5.MirrorCS"),sQuery(id+"F0.wireOp",EDGE,"E6.filletArc"),sQuery(id+"F0.wireOp",EDGE,"E7.filletArc"),sQuery(id+"F0.wireOp",EDGE,"E8.filletArc"),sQuery(id+"F0.wireOp",EDGE,"E9.filletArc"),sQuery(id+"F0.wireOp",EDGE,"E10.1.0"),sQuery(id+"F0.wireOp",EDGE,"E10.1.1"),sQuery(id+"F0.wireOp",EDGE,"E10.1.2"),sQuery(id+"F0.wireOp",EDGE,"E10.1.3"),sQuery(id+"F0.wireOp",EDGE,"E10.1.4"),sQuery(id+"F0.wireOp",EDGE,"E10.1.5"),sQuery(id+"F0.wireOp",EDGE,"E10.1.6"),sQuery(id+"F0.wireOp",EDGE,"E10.1.7"),sQuery(id+"F0.wireOp",EDGE,"E10.1.8"),sQuery(id+"F0.wireOp",EDGE,"E10.1.9"),sQuery(id+"F0.wireOp",EDGE,"E10.2.0"),sQuery(id+"F0.wireOp",EDGE,"E10.2.1"),sQuery(id+"F0.wireOp",EDGE,"E10.2.2"),sQuery(id+"F0.wireOp",EDGE,"E10.2.3"),sQuery(id+"F0.wireOp",EDGE,"E10.2.4"),sQuery(id+"F0.wireOp",EDGE,"E10.2.5"),sQuery(id+"F0.wireOp",EDGE,"E10.2.6"),sQuery(id+"F0.wireOp",EDGE,"E10.2.7"),sQuery(id+"F0.wireOp",EDGE,"E10.2.8"),sQuery(id+"F0.wireOp",EDGE,"E10.2.9"),sQuery(id+"F0.wireOp",EDGE,"E10.3.0"),sQuery(id+"F0.wireOp",EDGE,"E10.3.1"),sQuery(id+"F0.wireOp",EDGE,"E10.3.2"),sQuery(id+"F0.wireOp",EDGE,"E10.3.3"),sQuery(id+"F0.wireOp",EDGE,"E10.3.4"),sQuery(id+"F0.wireOp",EDGE,"E10.3.5"),sQuery(id+"F0.wireOp",EDGE,"E10.3.6"),sQuery(id+"F0.wireOp",EDGE,"E10.3.7"),sQuery(id+"F0.wireOp",EDGE,"E10.3.8"),sQuery(id+"F0.wireOp",EDGE,"E10.3.9"),sQuery(id+"F0.wireOp",EDGE,"E10.4.0"),sQuery(id+"F0.wireOp",EDGE,"E10.4.1"),sQuery(id+"F0.wireOp",EDGE,"E10.4.2"),sQuery(id+"F0.wireOp",EDGE,"E10.4.3"),sQuery(id+"F0.wireOp",EDGE,"E10.4.4"),sQuery(id+"F0.wireOp",EDGE,"E10.4.5"),sQuery(id+"F0.wireOp",EDGE,"E10.4.6"),sQuery(id+"F0.wireOp",EDGE,"E10.4.7"),sQuery(id+"F0.wireOp",EDGE,"E10.4.8"),sQuery(id+"F0.wireOp",EDGE,"E10.4.9"),sQuery(id+"F0.wireOp",EDGE,"E10.5.0"),sQuery(id+"F0.wireOp",EDGE,"E10.5.1"),sQuery(id+"F0.wireOp",EDGE,"E10.5.2"),sQuery(id+"F0.wireOp",EDGE,"E10.5.3"),sQuery(id+"F0.wireOp",EDGE,"E10.5.4"),sQuery(id+"F0.wireOp",EDGE,"E10.5.5"),sQuery(id+"F0.wireOp",EDGE,"E10.5.6"),sQuery(id+"F0.wireOp",EDGE,"E10.5.7"),sQuery(id+"F0.wireOp",EDGE,"E10.5.8"),sQuery(id+"F0.wireOp",EDGE,"E10.5.9"),sQuery(id+"F0.wireOp",EDGE,"E10.6.0"),sQuery(id+"F0.wireOp",EDGE,"E10.6.1"),sQuery(id+"F0.wireOp",EDGE,"E10.6.2"),sQuery(id+"F0.wireOp",EDGE,"E10.6.3"),sQuery(id+"F0.wireOp",EDGE,"E10.6.4"),sQuery(id+"F0.wireOp",EDGE,"E10.6.5"),sQuery(id+"F0.wireOp",EDGE,"E10.6.6"),sQuery(id+"F0.wireOp",EDGE,"E10.6.7"),sQuery(id+"F0.wireOp",EDGE,"E10.6.8"),sQuery(id+"F0.wireOp",EDGE,"E10.6.9"),sQuery(id+"F0.wireOp",EDGE,"E10.7.0"),sQuery(id+"F0.wireOp",EDGE,"E10.7.1"),sQuery(id+"F0.wireOp",EDGE,"E10.7.2"),sQuery(id+"F0.wireOp",EDGE,"E10.7.3"),sQuery(id+"F0.wireOp",EDGE,"E10.7.4"),sQuery(id+"F0.wireOp",EDGE,"E10.7.5"),sQuery(id+"F0.wireOp",EDGE,"E10.7.6"),sQuery(id+"F0.wireOp",EDGE,"E10.7.7"),sQuery(id+"F0.wireOp",EDGE,"E10.7.8"),sQuery(id+"F0.wireOp",EDGE,"E10.7.9"),sQuery(id+"F0.wireOp",EDGE,"E10.8.0"),sQuery(id+"F0.wireOp",EDGE,"E10.8.1"),sQuery(id+"F0.wireOp",EDGE,"E10.8.2"),sQuery(id+"F0.wireOp",EDGE,"E10.8.3"),sQuery(id+"F0.wireOp",EDGE,"E10.8.4"),sQuery(id+"F0.wireOp",EDGE,"E10.8.5"),sQuery(id+"F0.wireOp",EDGE,"E10.8.6"),sQuery(id+"F0.wireOp",EDGE,"E10.8.7"),sQuery(id+"F0.wireOp",EDGE,"E10.8.8"),sQuery(id+"F0.wireOp",EDGE,"E10.8.9"),sQuery(id+"F0.wireOp",EDGE,"E10.9.0"),sQuery(id+"F0.wireOp",EDGE,"E10.9.1"),sQuery(id+"F0.wireOp",EDGE,"E10.9.2"),sQuery(id+"F0.wireOp",EDGE,"E10.9.3"),sQuery(id+"F0.wireOp",EDGE,"E10.9.4"),sQuery(id+"F0.wireOp",EDGE,"E10.9.5"),sQuery(id+"F0.wireOp",EDGE,"E10.9.6"),sQuery(id+"F0.wireOp",EDGE,"E10.9.7"),sQuery(id+"F0.wireOp",EDGE,"E10.9.8"),sQuery(id+"F0.wireOp",EDGE,"E10.9.9"),sQuery(id+"F0.wireOp",EDGE,"E10.10.0"),sQuery(id+"F0.wireOp",EDGE,"E10.10.1"),sQuery(id+"F0.wireOp",EDGE,"E10.10.2"),sQuery(id+"F0.wireOp",EDGE,"E10.10.3"),sQuery(id+"F0.wireOp",EDGE,"E10.10.4"),sQuery(id+"F0.wireOp",EDGE,"E10.10.5"),sQuery(id+"F0.wireOp",EDGE,"E10.10.6"),sQuery(id+"F0.wireOp",EDGE,"E10.10.7"),sQuery(id+"F0.wireOp",EDGE,"E10.10.8"),sQuery(id+"F0.wireOp",EDGE,"E10.10.9"),sQuery(id+"F0.wireOp",EDGE,"E10.11.0"),sQuery(id+"F0.wireOp",EDGE,"E10.11.1"),sQuery(id+"F0.wireOp",EDGE,"E10.11.2"),sQuery(id+"F0.wireOp",EDGE,"E10.11.3"),sQuery(id+"F0.wireOp",EDGE,"E10.11.4"),sQuery(id+"F0.wireOp",EDGE,"E10.11.5"),sQuery(id+"F0.wireOp",EDGE,"E10.11.6"),sQuery(id+"F0.wireOp",EDGE,"E10.11.7"),sQuery(id+"F0.wireOp",EDGE,"E10.11.8"),sQuery(id+"F0.wireOp",EDGE,"E10.11.9"),sQuery(id+"F0.wireOp",EDGE,"E10.12.0"),sQuery(id+"F0.wireOp",EDGE,"E10.12.1"),sQuery(id+"F0.wireOp",EDGE,"E10.12.2"),sQuery(id+"F0.wireOp",EDGE,"E10.12.3"),sQuery(id+"F0.wireOp",EDGE,"E10.12.4"),sQuery(id+"F0.wireOp",EDGE,"E10.12.5"),sQuery(id+"F0.wireOp",EDGE,"E10.12.6"),sQuery(id+"F0.wireOp",EDGE,"E10.12.7"),sQuery(id+"F0.wireOp",EDGE,"E10.12.8"),sQuery(id+"F0.wireOp",EDGE,"E10.12.9"),sQuery(id+"F0.wireOp",EDGE,"E10.13.0"),sQuery(id+"F0.wireOp",EDGE,"E10.13.1"),sQuery(id+"F0.wireOp",EDGE,"E10.13.2"),sQuery(id+"F0.wireOp",EDGE,"E10.13.3"),sQuery(id+"F0.wireOp",EDGE,"E10.13.4"),sQuery(id+"F0.wireOp",EDGE,"E10.13.5"),sQuery(id+"F0.wireOp",EDGE,"E10.13.6"),sQuery(id+"F0.wireOp",EDGE,"E10.13.7"),sQuery(id+"F0.wireOp",EDGE,"E10.13.8"),sQuery(id+"F0.wireOp",EDGE,"E10.13.9"),sQuery(id+"F0.wireOp",EDGE,"E10.14.0"),sQuery(id+"F0.wireOp",EDGE,"E10.14.1"),sQuery(id+"F0.wireOp",EDGE,"E10.14.2"),sQuery(id+"F0.wireOp",EDGE,"E10.14.3"),sQuery(id+"F0.wireOp",EDGE,"E10.14.4"),sQuery(id+"F0.wireOp",EDGE,"E10.14.5"),sQuery(id+"F0.wireOp",EDGE,"E10.14.6"),sQuery(id+"F0.wireOp",EDGE,"E10.14.7"),sQuery(id+"F0.wireOp",EDGE,"E10.14.8"),sQuery(id+"F0.wireOp",EDGE,"E10.14.9"),sQuery(id+"F0.wireOp",EDGE,"E10.15.0"),sQuery(id+"F0.wireOp",EDGE,"E10.15.1"),sQuery(id+"F0.wireOp",EDGE,"E10.15.2"),sQuery(id+"F0.wireOp",EDGE,"E10.15.3"),sQuery(id+"F0.wireOp",EDGE,"E10.15.4"),sQuery(id+"F0.wireOp",EDGE,"E10.15.5"),sQuery(id+"F0.wireOp",EDGE,"E10.15.6"),sQuery(id+"F0.wireOp",EDGE,"E10.15.7"),sQuery(id+"F0.wireOp",EDGE,"E10.15.8"),sQuery(id+"F0.wireOp",EDGE,"E10.15.9"),sQuery(id+"F0.wireOp",EDGE,"E10.16.0"),sQuery(id+"F0.wireOp",EDGE,"E10.16.1"),sQuery(id+"F0.wireOp",EDGE,"E10.16.2"),sQuery(id+"F0.wireOp",EDGE,"E10.16.3"),sQuery(id+"F0.wireOp",EDGE,"E10.16.4"),sQuery(id+"F0.wireOp",EDGE,"E10.16.5"),sQuery(id+"F0.wireOp",EDGE,"E10.16.6"),sQuery(id+"F0.wireOp",EDGE,"E10.16.7"),sQuery(id+"F0.wireOp",EDGE,"E10.16.8"),sQuery(id+"F0.wireOp",EDGE,"E10.16.9"),sQuery(id+"F0.wireOp",EDGE,"E10.17.0"),sQuery(id+"F0.wireOp",EDGE,"E10.17.1"),sQuery(id+"F0.wireOp",EDGE,"E10.17.2"),sQuery(id+"F0.wireOp",EDGE,"E10.17.3"),sQuery(id+"F0.wireOp",EDGE,"E10.17.4"),sQuery(id+"F0.wireOp",EDGE,"E10.17.5"),sQuery(id+"F0.wireOp",EDGE,"E10.17.6"),sQuery(id+"F0.wireOp",EDGE,"E10.17.7"),sQuery(id+"F0.wireOp",EDGE,"E10.17.8"),sQuery(id+"F0.wireOp",EDGE,"E10.17.9"),sQuery(id+"F0.wireOp",EDGE,"E10.18.0"),sQuery(id+"F0.wireOp",EDGE,"E10.18.1"),sQuery(id+"F0.wireOp",EDGE,"E10.18.2"),sQuery(id+"F0.wireOp",EDGE,"E10.18.3"),sQuery(id+"F0.wireOp",EDGE,"E10.18.4"),sQuery(id+"F0.wireOp",EDGE,"E10.18.5"),sQuery(id+"F0.wireOp",EDGE,"E10.18.6"),sQuery(id+"F0.wireOp",EDGE,"E10.18.7"),sQuery(id+"F0.wireOp",EDGE,"E10.18.8"),sQuery(id+"F0.wireOp",EDGE,"E10.18.9"),sQuery(id+"F0.wireOp",EDGE,"E10.19.0"),sQuery(id+"F0.wireOp",EDGE,"E10.19.1"),sQuery(id+"F0.wireOp",EDGE,"E10.19.2"),sQuery(id+"F0.wireOp",EDGE,"E10.19.3"),sQuery(id+"F0.wireOp",EDGE,"E10.19.4"),sQuery(id+"F0.wireOp",EDGE,"E10.19.5"),sQuery(id+"F0.wireOp",EDGE,"E10.19.6"),sQuery(id+"F0.wireOp",EDGE,"E10.19.7"),sQuery(id+"F0.wireOp",EDGE,"E10.19.8"),sQuery(id+"F0.wireOp",EDGE,"E10.19.9"),sQuery(id+"F0.wireOp",EDGE,"E10.20.0"),sQuery(id+"F0.wireOp",EDGE,"E10.20.1"),sQuery(id+"F0.wireOp",EDGE,"E10.20.2"),sQuery(id+"F0.wireOp",EDGE,"E10.20.3"),sQuery(id+"F0.wireOp",EDGE,"E10.20.4"),sQuery(id+"F0.wireOp",EDGE,"E10.20.5"),sQuery(id+"F0.wireOp",EDGE,"E10.20.6"),sQuery(id+"F0.wireOp",EDGE,"E10.20.7"),sQuery(id+"F0.wireOp",EDGE,"E10.20.8"),sQuery(id+"F0.wireOp",EDGE,"E10.20.9"),sQuery(id+"F0.wireOp",EDGE,"E10.21.0"),sQuery(id+"F0.wireOp",EDGE,"E10.21.1"),sQuery(id+"F0.wireOp",EDGE,"E10.21.2"),sQuery(id+"F0.wireOp",EDGE,"E10.21.3"),sQuery(id+"F0.wireOp",EDGE,"E10.21.4"),sQuery(id+"F0.wireOp",EDGE,"E10.21.5"),sQuery(id+"F0.wireOp",EDGE,"E10.21.6"),sQuery(id+"F0.wireOp",EDGE,"E10.21.7"),sQuery(id+"F0.wireOp",EDGE,"E10.21.8"),sQuery(id+"F0.wireOp",EDGE,"E10.21.9"),sQuery(id+"F0.wireOp",EDGE,"E10.22.0"),sQuery(id+"F0.wireOp",EDGE,"E10.22.1"),sQuery(id+"F0.wireOp",EDGE,"E10.22.2"),sQuery(id+"F0.wireOp",EDGE,"E10.22.3"),sQuery(id+"F0.wireOp",EDGE,"E10.22.4"),sQuery(id+"F0.wireOp",EDGE,"E10.22.5"),sQuery(id+"F0.wireOp",EDGE,"E10.22.6"),sQuery(id+"F0.wireOp",EDGE,"E10.22.7"),sQuery(id+"F0.wireOp",EDGE,"E10.22.8"),sQuery(id+"F0.wireOp",EDGE,"E10.22.9"),sQuery(id+"F0.wireOp",EDGE,"E10.23.0"),sQuery(id+"F0.wireOp",EDGE,"E10.23.1"),sQuery(id+"F0.wireOp",EDGE,"E10.23.2"),sQuery(id+"F0.wireOp",EDGE,"E10.23.3"),sQuery(id+"F0.wireOp",EDGE,"E10.23.4"),sQuery(id+"F0.wireOp",EDGE,"E10.23.5"),sQuery(id+"F0.wireOp",EDGE,"E10.23.6"),sQuery(id+"F0.wireOp",EDGE,"E10.23.7"),sQuery(id+"F0.wireOp",EDGE,"E10.23.8"),sQuery(id+"F0.wireOp",EDGE,"E10.23.9"),sQuery(id+"F0.wireOp",EDGE,"E10.24.0"),sQuery(id+"F0.wireOp",EDGE,"E10.24.1"),sQuery(id+"F0.wireOp",EDGE,"E10.24.2"),sQuery(id+"F0.wireOp",EDGE,"E10.24.3"),sQuery(id+"F0.wireOp",EDGE,"E10.24.4"),sQuery(id+"F0.wireOp",EDGE,"E10.24.5"),sQuery(id+"F0.wireOp",EDGE,"E10.24.6"),sQuery(id+"F0.wireOp",EDGE,"E10.24.7"),sQuery(id+"F0.wireOp",EDGE,"E10.24.8"),sQuery(id+"F0.wireOp",EDGE,"E10.24.9"),sQuery(id+"F0.wireOp",EDGE,"E10.25.0"),sQuery(id+"F0.wireOp",EDGE,"E10.25.1"),sQuery(id+"F0.wireOp",EDGE,"E10.25.2"),sQuery(id+"F0.wireOp",EDGE,"E10.25.3"),sQuery(id+"F0.wireOp",EDGE,"E10.25.4"),sQuery(id+"F0.wireOp",EDGE,"E10.25.5"),sQuery(id+"F0.wireOp",EDGE,"E10.25.6"),sQuery(id+"F0.wireOp",EDGE,"E10.25.7"),sQuery(id+"F0.wireOp",EDGE,"E10.25.8"),sQuery(id+"F0.wireOp",EDGE,"E10.25.9"),sQuery(id+"F0.wireOp",EDGE,"E10.26.0"),sQuery(id+"F0.wireOp",EDGE,"E10.26.1"),sQuery(id+"F0.wireOp",EDGE,"E10.26.2"),sQuery(id+"F0.wireOp",EDGE,"E10.26.3"),sQuery(id+"F0.wireOp",EDGE,"E10.26.4"),sQuery(id+"F0.wireOp",EDGE,"E10.26.5"),sQuery(id+"F0.wireOp",EDGE,"E10.26.6"),sQuery(id+"F0.wireOp",EDGE,"E10.26.7"),sQuery(id+"F0.wireOp",EDGE,"E10.26.8"),sQuery(id+"F0.wireOp",EDGE,"E10.26.9"),sQuery(id+"F0.wireOp",EDGE,"E10.27.0"),sQuery(id+"F0.wireOp",EDGE,"E10.27.1"),sQuery(id+"F0.wireOp",EDGE,"E10.27.2"),sQuery(id+"F0.wireOp",EDGE,"E10.27.3"),sQuery(id+"F0.wireOp",EDGE,"E10.27.4"),sQuery(id+"F0.wireOp",EDGE,"E10.27.5"),sQuery(id+"F0.wireOp",EDGE,"E10.27.6"),sQuery(id+"F0.wireOp",EDGE,"E10.27.7"),sQuery(id+"F0.wireOp",EDGE,"E10.27.8"),sQuery(id+"F0.wireOp",EDGE,"E10.27.9"),sQuery(id+"F0.wireOp",EDGE,"E10.28.0"),sQuery(id+"F0.wireOp",EDGE,"E10.28.1"),sQuery(id+"F0.wireOp",EDGE,"E10.28.2"),sQuery(id+"F0.wireOp",EDGE,"E10.28.3"),sQuery(id+"F0.wireOp",EDGE,"E10.28.4"),sQuery(id+"F0.wireOp",EDGE,"E10.28.5"),sQuery(id+"F0.wireOp",EDGE,"E10.28.6"),sQuery(id+"F0.wireOp",EDGE,"E10.28.7"),sQuery(id+"F0.wireOp",EDGE,"E10.28.8"),sQuery(id+"F0.wireOp",EDGE,"E10.28.9"),sQuery(id+"F0.wireOp",EDGE,"E10.29.0"),sQuery(id+"F0.wireOp",EDGE,"E10.29.1"),sQuery(id+"F0.wireOp",EDGE,"E10.29.2"),sQuery(id+"F0.wireOp",EDGE,"E10.29.3"),sQuery(id+"F0.wireOp",EDGE,"E10.29.4"),sQuery(id+"F0.wireOp",EDGE,"E10.29.5"),sQuery(id+"F0.wireOp",EDGE,"E10.29.6"),sQuery(id+"F0.wireOp",EDGE,"E10.29.7"),sQuery(id+"F0.wireOp",EDGE,"E10.29.8"),sQuery(id+"F0.wireOp",EDGE,"E10.29.9"),sQuery(id+"F0.wireOp",EDGE,"E10.30.0"),sQuery(id+"F0.wireOp",EDGE,"E10.30.1"),sQuery(id+"F0.wireOp",EDGE,"E10.30.2"),sQuery(id+"F0.wireOp",EDGE,"E10.30.3"),sQuery(id+"F0.wireOp",EDGE,"E10.30.4"),sQuery(id+"F0.wireOp",EDGE,"E10.30.5"),sQuery(id+"F0.wireOp",EDGE,"E10.30.6"),sQuery(id+"F0.wireOp",EDGE,"E10.30.7"),sQuery(id+"F0.wireOp",EDGE,"E10.30.9"),sQuery(id+"F0.wireOp",EDGE,"E10.31.0"),sQuery(id+"F0.wireOp",EDGE,"E10.31.1"),sQuery(id+"F0.wireOp",EDGE,"E10.31.2"),sQuery(id+"F0.wireOp",EDGE,"E10.31.3"),sQuery(id+"F0.wireOp",EDGE,"E10.31.4"),sQuery(id+"F0.wireOp",EDGE,"E10.31.5"),sQuery(id+"F0.wireOp",EDGE,"E10.31.6"),sQuery(id+"F0.wireOp",EDGE,"E10.31.7"),sQuery(id+"F0.wireOp",EDGE,"E10.31.8"),sQuery(id+"F0.wireOp",EDGE,"E10.31.9"),sQuery(id+"F0.wireOp",EDGE,"E10.32.0"),sQuery(id+"F0.wireOp",EDGE,"E10.32.1"),sQuery(id+"F0.wireOp",EDGE,"E10.32.2"),sQuery(id+"F0.wireOp",EDGE,"E10.32.3"),sQuery(id+"F0.wireOp",EDGE,"E10.32.4"),sQuery(id+"F0.wireOp",EDGE,"E10.32.5"),sQuery(id+"F0.wireOp",EDGE,"E10.32.6"),sQuery(id+"F0.wireOp",EDGE,"E10.32.7"),sQuery(id+"F0.wireOp",EDGE,"E10.32.8"),sQuery(id+"F0.wireOp",EDGE,"E10.32.9"),sQuery(id+"F0.wireOp",EDGE,"E10.33.0"),sQuery(id+"F0.wireOp",EDGE,"E10.33.1"),sQuery(id+"F0.wireOp",EDGE,"E10.33.2"),sQuery(id+"F0.wireOp",EDGE,"E10.33.3"),sQuery(id+"F0.wireOp",EDGE,"E10.33.4"),sQuery(id+"F0.wireOp",EDGE,"E10.33.5"),sQuery(id+"F0.wireOp",EDGE,"E10.33.6"),sQuery(id+"F0.wireOp",EDGE,"E10.33.7"),sQuery(id+"F0.wireOp",EDGE,"E10.33.8"),sQuery(id+"F0.wireOp",EDGE,"E10.33.9"),sQuery(id+"F0.wireOp",EDGE,"E10.34.0"),sQuery(id+"F0.wireOp",EDGE,"E10.34.1"),sQuery(id+"F0.wireOp",EDGE,"E10.34.2"),sQuery(id+"F0.wireOp",EDGE,"E10.34.3"),sQuery(id+"F0.wireOp",EDGE,"E10.34.4"),sQuery(id+"F0.wireOp",EDGE,"E10.34.5"),sQuery(id+"F0.wireOp",EDGE,"E10.34.6"),sQuery(id+"F0.wireOp",EDGE,"E10.34.7"),sQuery(id+"F0.wireOp",EDGE,"E10.34.8"),sQuery(id+"F0.wireOp",EDGE,"E10.34.9"),sQuery(id+"F0.wireOp",EDGE,"E10.35.0"),sQuery(id+"F0.wireOp",EDGE,"E10.35.1"),sQuery(id+"F0.wireOp",EDGE,"E10.35.2"),sQuery(id+"F0.wireOp",EDGE,"E10.35.3"),sQuery(id+"F0.wireOp",EDGE,"E10.35.4"),sQuery(id+"F0.wireOp",EDGE,"E10.35.5"),sQuery(id+"F0.wireOp",EDGE,"E10.35.6"),sQuery(id+"F0.wireOp",EDGE,"E10.35.7"),sQuery(id+"F0.wireOp",EDGE,"E10.35.8"),sQuery(id+"F0.wireOp",EDGE,"E10.35.9"),sQuery(id+"F0.wireOp",EDGE,"E11.trimOffspring"),sQuery(id+"F0.wireOp",EDGE,"E12.trimOffspring"),sQuery(id+"F0.wireOp",EDGE,"E13.trimOffspring"),sQuery(id+"F0.wireOp",EDGE,"E14.trimOffspring"),sQuery(id+"F0.wireOp",EDGE,"E15.trimOffspring"),sQuery(id+"F0.wireOp",EDGE,"E16.trimOffspring"),sQuery(id+"F0.wireOp",EDGE,"E17.trimOffspring"),sQuery(id+"F0.wireOp",EDGE,"E18.trimOffspring"),sQuery(id+"F0.wireOp",EDGE,"E19.trimOffspring"),sQuery(id+"F0.wireOp",EDGE,"E20.trimOffspring"),sQuery(id+"F0.wireOp",EDGE,"E21.trimOffspring"),sQuery(id+"F0.wireOp",EDGE,"E22.trimOffspring"),sQuery(id+"F0.wireOp",EDGE,"E23.trimOffspring"),sQuery(id+"F0.wireOp",EDGE,"E24.trimOffspring"),sQuery(id+"F0.wireOp",EDGE,"E25.trimOffspring"),sQuery(id+"F0.wireOp",EDGE,"E26.trimOffspring"),sQuery(id+"F0.wireOp",EDGE,"E27.trimOffspring"),sQuery(id+"F0.wireOp",EDGE,"E28.trimOffspring"),sQuery(id+"F0.wireOp",EDGE,"E29.trimOffspring"),sQuery(id+"F0.wireOp",EDGE,"E30.trimOffspring"),sQuery(id+"F0.wireOp",EDGE,"E31.trimOffspring"),sQuery(id+"F0.wireOp",EDGE,"E32.trimOffspring"),sQuery(id+"F0.wireOp",EDGE,"E33.trimOffspring"),sQuery(id+"F0.wireOp",EDGE,"E34.trimOffspring"),sQuery(id+"F0.wireOp",EDGE,"E35.trimOffspring"),sQuery(id+"F0.wireOp",EDGE,"E36.trimOffspring"),sQuery(id+"F0.wireOp",EDGE,"E37.trimOffspring"),sQuery(id+"F0.wireOp",EDGE,"E38.trimOffspring"),sQuery(id+"F0.wireOp",EDGE,"E39"),sQuery(id+"F0.wireOp",EDGE,"E40.trimOffspring"),sQuery(id+"F0.wireOp",EDGE,"E41"),sQuery(id+"F0.wireOp",EDGE,"E42"),sQuery(id+"F0.wireOp",EDGE,"E43"),sQuery(id+"F0.wireOp",EDGE,"E44"),sQuery(id+"F0.wireOp",EDGE,"E45"),sQuery(id+"F0.wireOp",EDGE,"E46"),sQuery(id+"F0.wireOp",EDGE,"E47")])],"isStart":false});
            shell(context, id + "F4", {"entities" : qUnion([Q0]), "thickness" : 6.35 * mm});
        }
        {
            var Q0;
            Q0=qCreatedBy(makeId("Right.planeOp"),FACE);
            cPlane(context, id + "F5", {"entities" : qUnion([Q0]), "cplaneType" : CPlaneType.OFFSET, "offset" : 9.52 * mm, "width" : 152.4 * mm, "height" : 152.4 * mm});
        }
        {
            var Q0;
            Q0=qCreatedBy(id+"F5.planeOp",FACE);
            var sketch = newSketch(context, id + "F6", { "sketchPlane" : qUnion([Q0])});
            skCircle(sketch, "E49", {"center": v(-9.53, 0) * mm, "radius": 1.13 * mm});
            skSolve(sketch);
        }
        {
            var Q0;
            Q0 = qSketchRegion(id + "F6", true);
            extrude(context, id + "F7", {"entities" : qUnion([Q0]), "operationType" : NewBodyOperationType.REMOVE, "oppositeDirection" : true, "depth" : 9.52 * mm});
        }
    });
